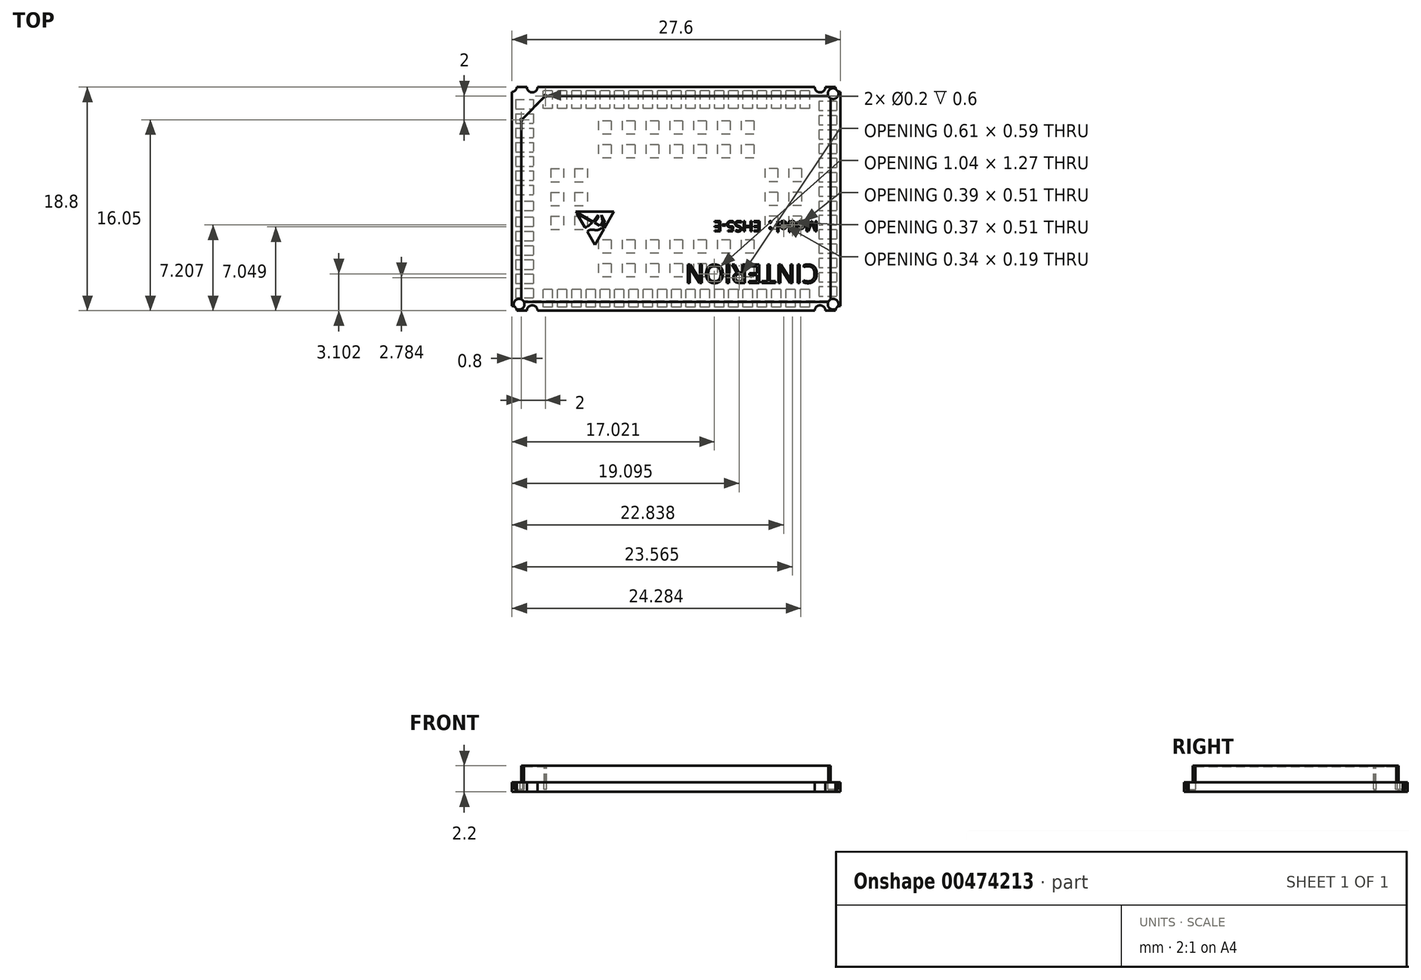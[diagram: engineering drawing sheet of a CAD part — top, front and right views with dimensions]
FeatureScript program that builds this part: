
annotation { "Feature Type Name" : "Feature", "Feature Type Description" : "" }
export const myFeature = defineFeature(function(context is Context, id is Id, definition is map)
    precondition{}
    {
        {
            var Q0;
            Q0=qCreatedBy(makeId("Top.planeOp"),FACE);
            var sketch = newSketch(context, id + "F0", { "sketchPlane" : qUnion([Q0])});
            skLineSegment(sketch, "E0.bottom", {"start": v(13, -8.65) * mm, "end": v(-13, -8.65) * mm});
            skLineSegment(sketch, "E0.top", {"start": v(13, 8.65) * mm, "end": v(-13, 8.65) * mm});
            skLineSegment(sketch, "E0.left", {"start": v(13, -8.65) * mm, "end": v(13, 8.65) * mm});
            skLineSegment(sketch, "E0.right", {"start": v(-13, -8.65) * mm, "end": v(-13, 8.65) * mm});
            skPoint(sketch, "E0.middle", {"position": v(0, 0) * mm});
            skLineSegment(sketch, "E1", {"start": v(-13, 6.65) * mm, "end": v(-11, 8.65) * mm});
            skLineSegment(sketch, "E2", {"start": v(-13, -9.4) * mm, "end": v(-13.8, -9.4) * mm});
            skLineSegment(sketch, "E3", {"start": v(-13.8, -9.4) * mm, "end": v(-13.8, 9.4) * mm});
            skLineSegment(sketch, "E4", {"start": v(-13.8, 9.4) * mm, "end": v(13.8, 9.4) * mm});
            skLineSegment(sketch, "E5", {"start": v(13.8, 9.4) * mm, "end": v(13.8, -9.4) * mm});
            skLineSegment(sketch, "E6", {"start": v(13.8, -9.4) * mm, "end": v(-13.8, -9.4) * mm});
            skArc(sketch, "E7", {"start": v(-13.8, 9) * mm, "mid": v(-13.52, 9.12) * mm, "end": v(-13.4, 9.4) * mm});
            skLineSegment(sketch, "E8", {"start": v(-13.8, 9.4) * mm, "end": v(-12.1, 9.4) * mm});
            skArc(sketch, "E9", {"start": v(-11.65, 9.4) * mm, "mid": v(-12.1, 8.95) * mm, "end": v(-12.55, 9.4) * mm});
            skPoint(sketch, "E10.startSnap0", {"position": v(-12.1, 8.95) * mm});
            skArc(sketch, "E11", {"start": v(13.8, 9) * mm, "mid": v(13.52, 9.12) * mm, "end": v(13.4, 9.4) * mm});
            skArc(sketch, "E12", {"start": v(13.4, -9.4) * mm, "mid": v(13.52, -9.12) * mm, "end": v(13.8, -9) * mm});
            skArc(sketch, "E13", {"start": v(-13.8, -9) * mm, "mid": v(-13.52, -9.12) * mm, "end": v(-13.4, -9.4) * mm});
            skLineSegment(sketch, "E14", {"start": v(-13.8, -9.4) * mm, "end": v(-12.1, -9.4) * mm});
            skLineSegment(sketch, "E15", {"start": v(13.8, -9.4) * mm, "end": v(12.1, -9.4) * mm});
            skLineSegment(sketch, "E16", {"start": v(13.8, 9.4) * mm, "end": v(12.1, 9.4) * mm});
            skArc(sketch, "E17", {"start": v(11.65, 9.4) * mm, "mid": v(12.1, 8.95) * mm, "end": v(12.55, 9.4) * mm});
            skArc(sketch, "E18", {"start": v(12.55, -9.4) * mm, "mid": v(12.1, -8.95) * mm, "end": v(11.65, -9.4) * mm});
            skArc(sketch, "E19", {"start": v(-11.65, -9.4) * mm, "mid": v(-12.1, -8.95) * mm, "end": v(-12.55, -9.4) * mm});
            skSolve(sketch);
        }
        {
            var Q0;
            {var subQ1=sQuery(id+"F0.wireOp",EDGE,"E0.bottom");Q0=makeQuery(id+"F0.imprint","IMPRINT",FACE,{"disambiguationData":[TD([[makeQuery(id+"F0.imprint","IMPRINT",EDGE,{"derivedFrom":subQ1}),-1.0]])]});}
            extrude(context, id + "F1", {"entities" : qUnion([Q0]), "depth" : 1.4 * mm});
        }
        {
            var Q0;
            {var subQ14=sQuery(id+"F0.wireOp",EDGE,"E0.bottom");Q0=makeQuery(id+"F0.imprint","IMPRINT",FACE,{"disambiguationData":[TD([[makeQuery(id+"F0.imprint","IMPRINT",EDGE,{"derivedFrom":subQ14}),1.0]])]});}
            var Q1;
            {var subQ1=sQuery(id+"F0.wireOp",EDGE,"E0.bottom");Q1=makeQuery(id+"F0.imprint","IMPRINT",FACE,{"disambiguationData":[TD([[makeQuery(id+"F0.imprint","IMPRINT",EDGE,{"derivedFrom":subQ1}),-1.0]])]});}
            var Q2;
            {var subQ3=sQuery(id+"F0.wireOp",EDGE,"E1");Q2=makeQuery(id+"F0.imprint","IMPRINT",FACE,{"disambiguationData":[TD([[makeQuery(id+"F0.imprint","IMPRINT",EDGE,{"derivedFrom":subQ3}),1.0]])]});}
            extrude(context, id + "F2", {"entities" : qUnion([Q0, Q1, Q2]), "oppositeDirection" : true, "depth" : 0.8 * mm});
        }
        {
            var Q0;
            Q0=makeQuery(id+"F1.opExtrude","CAP_FACE",FACE,{"disambiguationData":[OSD([sQuery(id+"F0.wireOp",EDGE,"E0.bottom"),sQuery(id+"F0.wireOp",EDGE,"E0.top"),sQuery(id+"F0.wireOp",EDGE,"E0.left"),sQuery(id+"F0.wireOp",EDGE,"E0.right"),sQuery(id+"F0.wireOp",EDGE,"E1")])],"isStart":true});
            shell(context, id + "F3", {"entities" : qUnion([Q0]), "thickness" : 0.05 * mm});
        }
        {
            var Q0;
            Q0=makeQuery(id+"F1.opExtrude","CAP_FACE",FACE,{"disambiguationData":[OSD([sQuery(id+"F0.wireOp",EDGE,"E0.bottom"),sQuery(id+"F0.wireOp",EDGE,"E0.top"),sQuery(id+"F0.wireOp",EDGE,"E0.left"),sQuery(id+"F0.wireOp",EDGE,"E0.right"),sQuery(id+"F0.wireOp",EDGE,"E1")])],"isStart":false});
            var sketch = newSketch(context, id + "F4", { "sketchPlane" : qUnion([Q0])});
            skCircle(sketch, "E20", {"center": v(13.2, -8.85) * mm, "radius": 0.45 * mm});
            skCircle(sketch, "E21.1.0.0", {"center": v(-13.2, -8.85) * mm, "radius": 0.45 * mm});
            skLineSegment(sketch, "E21.direction1", {"start": v(13.2, -8.85) * mm, "end": v(-13.2, -8.85) * mm, "construction": true});
            skCircle(sketch, "E22", {"center": v(-13, 6.65) * mm, "radius": 0.1 * mm});
            skCircle(sketch, "E23", {"center": v(-11, 8.65) * mm, "radius": 0.1 * mm});
            skCircle(sketch, "E24.0.1.0", {"center": v(13.2, 8.85) * mm, "radius": 0.45 * mm});
            skLineSegment(sketch, "E24.direction1", {"start": v(13.2, -8.85) * mm, "end": v(38.2, -8.85) * mm, "construction": true});
            skLineSegment(sketch, "E24.direction2", {"start": v(13.2, -8.85) * mm, "end": v(13.2, 8.85) * mm, "construction": true});
            skSolve(sketch);
        }
        {
            var Q0;
            Q0 = qSketchRegion(id + "F4", true);
            extrude(context, id + "F5", {"entities" : qUnion([Q0]), "operationType" : NewBodyOperationType.REMOVE, "oppositeDirection" : true, "depth" : 2 * mm});
        }
        {
            var Q0;
            Q0=makeQuery(id+"F2.opExtrude","CAP_FACE",FACE,{"disambiguationData":[OSD([sQuery(id+"F0.wireOp",EDGE,"E3"),sQuery(id+"F0.wireOp",EDGE,"E4"),sQuery(id+"F0.wireOp",EDGE,"E5"),sQuery(id+"F0.wireOp",EDGE,"E6"),sQuery(id+"F0.wireOp",EDGE,"E7"),sQuery(id+"F0.wireOp",EDGE,"E8"),sQuery(id+"F0.wireOp",EDGE,"E9"),sQuery(id+"F0.wireOp",EDGE,"E11"),sQuery(id+"F0.wireOp",EDGE,"E12"),sQuery(id+"F0.wireOp",EDGE,"E13"),sQuery(id+"F0.wireOp",EDGE,"E14"),sQuery(id+"F0.wireOp",EDGE,"E15"),sQuery(id+"F0.wireOp",EDGE,"E16"),sQuery(id+"F0.wireOp",EDGE,"E17"),sQuery(id+"F0.wireOp",EDGE,"E18"),sQuery(id+"F0.wireOp",EDGE,"E19")])],"isStart":false});
            var sketch = newSketch(context, id + "F6", { "sketchPlane" : qUnion([Q0])});
            skLineSegment(sketch, "E25.bottom", {"start": v(0.4, 7.6) * mm, "end": v(-0.4, 7.6) * mm});
            skLineSegment(sketch, "E25.top", {"start": v(0.4, 9.1) * mm, "end": v(-0.4, 9.1) * mm});
            skLineSegment(sketch, "E25.left", {"start": v(0.4, 7.6) * mm, "end": v(0.4, 9.1) * mm});
            skLineSegment(sketch, "E25.right", {"start": v(-0.4, 7.6) * mm, "end": v(-0.4, 9.1) * mm});
            skPoint(sketch, "E25.middle", {"position": v(0, 8.35) * mm});
            skLineSegment(sketch, "E26.bottom", {"start": v(0.4, -9.1) * mm, "end": v(-0.4, -9.1) * mm});
            skLineSegment(sketch, "E26.top", {"start": v(0.4, -7.6) * mm, "end": v(-0.4, -7.6) * mm});
            skLineSegment(sketch, "E26.left", {"start": v(0.4, -9.1) * mm, "end": v(0.4, -7.6) * mm});
            skLineSegment(sketch, "E26.right", {"start": v(-0.4, -9.1) * mm, "end": v(-0.4, -7.6) * mm});
            skPoint(sketch, "E26.middle", {"position": v(0, -8.35) * mm});
            skLineSegment(sketch, "E27.1.0.0", {"start": v(-1.6, 7.6) * mm, "end": v(-1.6, 9.1) * mm});
            skLineSegment(sketch, "E27.1.0.1", {"start": v(-0.8, 7.6) * mm, "end": v(-0.8, 9.1) * mm});
            skLineSegment(sketch, "E27.1.0.2", {"start": v(-0.8, 9.1) * mm, "end": v(-1.6, 9.1) * mm});
            skLineSegment(sketch, "E27.1.0.3", {"start": v(-0.8, 7.6) * mm, "end": v(-1.6, 7.6) * mm});
            skPoint(sketch, "E27.1.0.4", {"position": v(-1.2, 8.35) * mm});
            skLineSegment(sketch, "E27.1.0.5", {"start": v(-1.6, -9.1) * mm, "end": v(-1.6, -7.6) * mm});
            skLineSegment(sketch, "E27.1.0.6", {"start": v(-0.8, -9.1) * mm, "end": v(-0.8, -7.6) * mm});
            skLineSegment(sketch, "E27.1.0.7", {"start": v(-0.8, -7.6) * mm, "end": v(-1.6, -7.6) * mm});
            skLineSegment(sketch, "E27.1.0.8", {"start": v(-0.8, -9.1) * mm, "end": v(-1.6, -9.1) * mm});
            skPoint(sketch, "E27.1.0.9", {"position": v(-1.2, -8.35) * mm});
            skLineSegment(sketch, "E27.2.0.0", {"start": v(-2.8, 7.6) * mm, "end": v(-2.8, 9.1) * mm});
            skLineSegment(sketch, "E27.2.0.1", {"start": v(-2, 7.6) * mm, "end": v(-2, 9.1) * mm});
            skLineSegment(sketch, "E27.2.0.2", {"start": v(-2, 9.1) * mm, "end": v(-2.8, 9.1) * mm});
            skLineSegment(sketch, "E27.2.0.3", {"start": v(-2, 7.6) * mm, "end": v(-2.8, 7.6) * mm});
            skPoint(sketch, "E27.2.0.4", {"position": v(-2.4, 8.35) * mm});
            skLineSegment(sketch, "E27.2.0.5", {"start": v(-2.8, -9.1) * mm, "end": v(-2.8, -7.6) * mm});
            skLineSegment(sketch, "E27.2.0.6", {"start": v(-2, -9.1) * mm, "end": v(-2, -7.6) * mm});
            skLineSegment(sketch, "E27.2.0.7", {"start": v(-2, -7.6) * mm, "end": v(-2.8, -7.6) * mm});
            skLineSegment(sketch, "E27.2.0.8", {"start": v(-2, -9.1) * mm, "end": v(-2.8, -9.1) * mm});
            skPoint(sketch, "E27.2.0.9", {"position": v(-2.4, -8.35) * mm});
            skLineSegment(sketch, "E27.3.0.0", {"start": v(-4, 7.6) * mm, "end": v(-4, 9.1) * mm});
            skLineSegment(sketch, "E27.3.0.1", {"start": v(-3.2, 7.6) * mm, "end": v(-3.2, 9.1) * mm});
            skLineSegment(sketch, "E27.3.0.2", {"start": v(-3.2, 9.1) * mm, "end": v(-4, 9.1) * mm});
            skLineSegment(sketch, "E27.3.0.3", {"start": v(-3.2, 7.6) * mm, "end": v(-4, 7.6) * mm});
            skPoint(sketch, "E27.3.0.4", {"position": v(-3.6, 8.35) * mm});
            skLineSegment(sketch, "E27.3.0.5", {"start": v(-4, -9.1) * mm, "end": v(-4, -7.6) * mm});
            skLineSegment(sketch, "E27.3.0.6", {"start": v(-3.2, -9.1) * mm, "end": v(-3.2, -7.6) * mm});
            skLineSegment(sketch, "E27.3.0.7", {"start": v(-3.2, -7.6) * mm, "end": v(-4, -7.6) * mm});
            skLineSegment(sketch, "E27.3.0.8", {"start": v(-3.2, -9.1) * mm, "end": v(-4, -9.1) * mm});
            skPoint(sketch, "E27.3.0.9", {"position": v(-3.6, -8.35) * mm});
            skLineSegment(sketch, "E27.4.0.0", {"start": v(-5.2, 7.6) * mm, "end": v(-5.2, 9.1) * mm});
            skLineSegment(sketch, "E27.4.0.1", {"start": v(-4.4, 7.6) * mm, "end": v(-4.4, 9.1) * mm});
            skLineSegment(sketch, "E27.4.0.2", {"start": v(-4.4, 9.1) * mm, "end": v(-5.2, 9.1) * mm});
            skLineSegment(sketch, "E27.4.0.3", {"start": v(-4.4, 7.6) * mm, "end": v(-5.2, 7.6) * mm});
            skPoint(sketch, "E27.4.0.4", {"position": v(-4.8, 8.35) * mm});
            skLineSegment(sketch, "E27.4.0.5", {"start": v(-5.2, -9.1) * mm, "end": v(-5.2, -7.6) * mm});
            skLineSegment(sketch, "E27.4.0.6", {"start": v(-4.4, -9.1) * mm, "end": v(-4.4, -7.6) * mm});
            skLineSegment(sketch, "E27.4.0.7", {"start": v(-4.4, -7.6) * mm, "end": v(-5.2, -7.6) * mm});
            skLineSegment(sketch, "E27.4.0.8", {"start": v(-4.4, -9.1) * mm, "end": v(-5.2, -9.1) * mm});
            skPoint(sketch, "E27.4.0.9", {"position": v(-4.8, -8.35) * mm});
            skLineSegment(sketch, "E27.5.0.0", {"start": v(-6.4, 7.6) * mm, "end": v(-6.4, 9.1) * mm});
            skLineSegment(sketch, "E27.5.0.1", {"start": v(-5.6, 7.6) * mm, "end": v(-5.6, 9.1) * mm});
            skLineSegment(sketch, "E27.5.0.2", {"start": v(-5.6, 9.1) * mm, "end": v(-6.4, 9.1) * mm});
            skLineSegment(sketch, "E27.5.0.3", {"start": v(-5.6, 7.6) * mm, "end": v(-6.4, 7.6) * mm});
            skPoint(sketch, "E27.5.0.4", {"position": v(-6, 8.35) * mm});
            skLineSegment(sketch, "E27.5.0.5", {"start": v(-6.4, -9.1) * mm, "end": v(-6.4, -7.6) * mm});
            skLineSegment(sketch, "E27.5.0.6", {"start": v(-5.6, -9.1) * mm, "end": v(-5.6, -7.6) * mm});
            skLineSegment(sketch, "E27.5.0.7", {"start": v(-5.6, -7.6) * mm, "end": v(-6.4, -7.6) * mm});
            skLineSegment(sketch, "E27.5.0.8", {"start": v(-5.6, -9.1) * mm, "end": v(-6.4, -9.1) * mm});
            skPoint(sketch, "E27.5.0.9", {"position": v(-6, -8.35) * mm});
            skLineSegment(sketch, "E27.6.0.0", {"start": v(-7.6, 7.6) * mm, "end": v(-7.6, 9.1) * mm});
            skLineSegment(sketch, "E27.6.0.1", {"start": v(-6.8, 7.6) * mm, "end": v(-6.8, 9.1) * mm});
            skLineSegment(sketch, "E27.6.0.2", {"start": v(-6.8, 9.1) * mm, "end": v(-7.6, 9.1) * mm});
            skLineSegment(sketch, "E27.6.0.3", {"start": v(-6.8, 7.6) * mm, "end": v(-7.6, 7.6) * mm});
            skPoint(sketch, "E27.6.0.4", {"position": v(-7.2, 8.35) * mm});
            skLineSegment(sketch, "E27.6.0.5", {"start": v(-7.6, -9.1) * mm, "end": v(-7.6, -7.6) * mm});
            skLineSegment(sketch, "E27.6.0.6", {"start": v(-6.8, -9.1) * mm, "end": v(-6.8, -7.6) * mm});
            skLineSegment(sketch, "E27.6.0.7", {"start": v(-6.8, -7.6) * mm, "end": v(-7.6, -7.6) * mm});
            skLineSegment(sketch, "E27.6.0.8", {"start": v(-6.8, -9.1) * mm, "end": v(-7.6, -9.1) * mm});
            skPoint(sketch, "E27.6.0.9", {"position": v(-7.2, -8.35) * mm});
            skLineSegment(sketch, "E27.7.0.0", {"start": v(-8.8, 7.6) * mm, "end": v(-8.8, 9.1) * mm});
            skLineSegment(sketch, "E27.7.0.1", {"start": v(-8, 7.6) * mm, "end": v(-8, 9.1) * mm});
            skLineSegment(sketch, "E27.7.0.2", {"start": v(-8, 9.1) * mm, "end": v(-8.8, 9.1) * mm});
            skLineSegment(sketch, "E27.7.0.3", {"start": v(-8, 7.6) * mm, "end": v(-8.8, 7.6) * mm});
            skPoint(sketch, "E27.7.0.4", {"position": v(-8.4, 8.35) * mm});
            skLineSegment(sketch, "E27.7.0.5", {"start": v(-8.8, -9.1) * mm, "end": v(-8.8, -7.6) * mm});
            skLineSegment(sketch, "E27.7.0.6", {"start": v(-8, -9.1) * mm, "end": v(-8, -7.6) * mm});
            skLineSegment(sketch, "E27.7.0.7", {"start": v(-8, -7.6) * mm, "end": v(-8.8, -7.6) * mm});
            skLineSegment(sketch, "E27.7.0.8", {"start": v(-8, -9.1) * mm, "end": v(-8.8, -9.1) * mm});
            skPoint(sketch, "E27.7.0.9", {"position": v(-8.4, -8.35) * mm});
            skLineSegment(sketch, "E27.8.0.0", {"start": v(-10, 7.6) * mm, "end": v(-10, 9.1) * mm});
            skLineSegment(sketch, "E27.8.0.1", {"start": v(-9.2, 7.6) * mm, "end": v(-9.2, 9.1) * mm});
            skLineSegment(sketch, "E27.8.0.2", {"start": v(-9.2, 9.1) * mm, "end": v(-10, 9.1) * mm});
            skLineSegment(sketch, "E27.8.0.3", {"start": v(-9.2, 7.6) * mm, "end": v(-10, 7.6) * mm});
            skPoint(sketch, "E27.8.0.4", {"position": v(-9.6, 8.35) * mm});
            skLineSegment(sketch, "E27.8.0.5", {"start": v(-10, -9.1) * mm, "end": v(-10, -7.6) * mm});
            skLineSegment(sketch, "E27.8.0.6", {"start": v(-9.2, -9.1) * mm, "end": v(-9.2, -7.6) * mm});
            skLineSegment(sketch, "E27.8.0.7", {"start": v(-9.2, -7.6) * mm, "end": v(-10, -7.6) * mm});
            skLineSegment(sketch, "E27.8.0.8", {"start": v(-9.2, -9.1) * mm, "end": v(-10, -9.1) * mm});
            skPoint(sketch, "E27.8.0.9", {"position": v(-9.6, -8.35) * mm});
            skLineSegment(sketch, "E27.9.0.0", {"start": v(-11.2, 7.6) * mm, "end": v(-11.2, 9.1) * mm});
            skLineSegment(sketch, "E27.9.0.1", {"start": v(-10.4, 7.6) * mm, "end": v(-10.4, 9.1) * mm});
            skLineSegment(sketch, "E27.9.0.2", {"start": v(-10.4, 9.1) * mm, "end": v(-11.2, 9.1) * mm});
            skLineSegment(sketch, "E27.9.0.3", {"start": v(-10.4, 7.6) * mm, "end": v(-11.2, 7.6) * mm});
            skPoint(sketch, "E27.9.0.4", {"position": v(-10.8, 8.35) * mm});
            skLineSegment(sketch, "E27.9.0.5", {"start": v(-11.2, -9.1) * mm, "end": v(-11.2, -7.6) * mm});
            skLineSegment(sketch, "E27.9.0.6", {"start": v(-10.4, -9.1) * mm, "end": v(-10.4, -7.6) * mm});
            skLineSegment(sketch, "E27.9.0.7", {"start": v(-10.4, -7.6) * mm, "end": v(-11.2, -7.6) * mm});
            skLineSegment(sketch, "E27.9.0.8", {"start": v(-10.4, -9.1) * mm, "end": v(-11.2, -9.1) * mm});
            skPoint(sketch, "E27.9.0.9", {"position": v(-10.8, -8.35) * mm});
            skLineSegment(sketch, "E27.direction1", {"start": v(-0.4, -9.1) * mm, "end": v(-1.6, -9.1) * mm, "construction": true});
            skLineSegment(sketch, "E28.1.0.0", {"start": v(0.8, 7.6) * mm, "end": v(0.8, 9.1) * mm});
            skLineSegment(sketch, "E28.1.0.1", {"start": v(1.6, 7.6) * mm, "end": v(1.6, 9.1) * mm});
            skLineSegment(sketch, "E28.1.0.2", {"start": v(1.6, 9.1) * mm, "end": v(0.8, 9.1) * mm});
            skLineSegment(sketch, "E28.1.0.3", {"start": v(1.6, 7.6) * mm, "end": v(0.8, 7.6) * mm});
            skPoint(sketch, "E28.1.0.4", {"position": v(1.2, 8.35) * mm});
            skLineSegment(sketch, "E28.1.0.5", {"start": v(1.6, -9.1) * mm, "end": v(0.8, -9.1) * mm});
            skLineSegment(sketch, "E28.1.0.6", {"start": v(1.6, -7.6) * mm, "end": v(0.8, -7.6) * mm});
            skPoint(sketch, "E28.1.0.7", {"position": v(1.2, -8.35) * mm});
            skLineSegment(sketch, "E28.1.0.8", {"start": v(0.8, -9.1) * mm, "end": v(0.8, -7.6) * mm});
            skLineSegment(sketch, "E28.1.0.9", {"start": v(1.6, -9.1) * mm, "end": v(1.6, -7.6) * mm});
            skLineSegment(sketch, "E28.2.0.0", {"start": v(2, 7.6) * mm, "end": v(2, 9.1) * mm});
            skLineSegment(sketch, "E28.2.0.1", {"start": v(2.8, 7.6) * mm, "end": v(2.8, 9.1) * mm});
            skLineSegment(sketch, "E28.2.0.2", {"start": v(2.8, 9.1) * mm, "end": v(2, 9.1) * mm});
            skLineSegment(sketch, "E28.2.0.3", {"start": v(2.8, 7.6) * mm, "end": v(2, 7.6) * mm});
            skPoint(sketch, "E28.2.0.4", {"position": v(2.4, 8.35) * mm});
            skLineSegment(sketch, "E28.2.0.5", {"start": v(2.8, -9.1) * mm, "end": v(2, -9.1) * mm});
            skLineSegment(sketch, "E28.2.0.6", {"start": v(2.8, -7.6) * mm, "end": v(2, -7.6) * mm});
            skPoint(sketch, "E28.2.0.7", {"position": v(2.4, -8.35) * mm});
            skLineSegment(sketch, "E28.2.0.8", {"start": v(2, -9.1) * mm, "end": v(2, -7.6) * mm});
            skLineSegment(sketch, "E28.2.0.9", {"start": v(2.8, -9.1) * mm, "end": v(2.8, -7.6) * mm});
            skLineSegment(sketch, "E28.3.0.0", {"start": v(3.2, 7.6) * mm, "end": v(3.2, 9.1) * mm});
            skLineSegment(sketch, "E28.3.0.1", {"start": v(4, 7.6) * mm, "end": v(4, 9.1) * mm});
            skLineSegment(sketch, "E28.3.0.2", {"start": v(4, 9.1) * mm, "end": v(3.2, 9.1) * mm});
            skLineSegment(sketch, "E28.3.0.3", {"start": v(4, 7.6) * mm, "end": v(3.2, 7.6) * mm});
            skPoint(sketch, "E28.3.0.4", {"position": v(3.6, 8.35) * mm});
            skLineSegment(sketch, "E28.3.0.5", {"start": v(4, -9.1) * mm, "end": v(3.2, -9.1) * mm});
            skLineSegment(sketch, "E28.3.0.6", {"start": v(4, -7.6) * mm, "end": v(3.2, -7.6) * mm});
            skPoint(sketch, "E28.3.0.7", {"position": v(3.6, -8.35) * mm});
            skLineSegment(sketch, "E28.3.0.8", {"start": v(3.2, -9.1) * mm, "end": v(3.2, -7.6) * mm});
            skLineSegment(sketch, "E28.3.0.9", {"start": v(4, -9.1) * mm, "end": v(4, -7.6) * mm});
            skLineSegment(sketch, "E28.4.0.0", {"start": v(4.4, 7.6) * mm, "end": v(4.4, 9.1) * mm});
            skLineSegment(sketch, "E28.4.0.1", {"start": v(5.2, 7.6) * mm, "end": v(5.2, 9.1) * mm});
            skLineSegment(sketch, "E28.4.0.2", {"start": v(5.2, 9.1) * mm, "end": v(4.4, 9.1) * mm});
            skLineSegment(sketch, "E28.4.0.3", {"start": v(5.2, 7.6) * mm, "end": v(4.4, 7.6) * mm});
            skPoint(sketch, "E28.4.0.4", {"position": v(4.8, 8.35) * mm});
            skLineSegment(sketch, "E28.4.0.5", {"start": v(5.2, -9.1) * mm, "end": v(4.4, -9.1) * mm});
            skLineSegment(sketch, "E28.4.0.6", {"start": v(5.2, -7.6) * mm, "end": v(4.4, -7.6) * mm});
            skPoint(sketch, "E28.4.0.7", {"position": v(4.8, -8.35) * mm});
            skLineSegment(sketch, "E28.4.0.8", {"start": v(4.4, -9.1) * mm, "end": v(4.4, -7.6) * mm});
            skLineSegment(sketch, "E28.4.0.9", {"start": v(5.2, -9.1) * mm, "end": v(5.2, -7.6) * mm});
            skLineSegment(sketch, "E28.5.0.0", {"start": v(5.6, 7.6) * mm, "end": v(5.6, 9.1) * mm});
            skLineSegment(sketch, "E28.5.0.1", {"start": v(6.4, 7.6) * mm, "end": v(6.4, 9.1) * mm});
            skLineSegment(sketch, "E28.5.0.2", {"start": v(6.4, 9.1) * mm, "end": v(5.6, 9.1) * mm});
            skLineSegment(sketch, "E28.5.0.3", {"start": v(6.4, 7.6) * mm, "end": v(5.6, 7.6) * mm});
            skPoint(sketch, "E28.5.0.4", {"position": v(6, 8.35) * mm});
            skLineSegment(sketch, "E28.5.0.5", {"start": v(6.4, -9.1) * mm, "end": v(5.6, -9.1) * mm});
            skLineSegment(sketch, "E28.5.0.6", {"start": v(6.4, -7.6) * mm, "end": v(5.6, -7.6) * mm});
            skPoint(sketch, "E28.5.0.7", {"position": v(6, -8.35) * mm});
            skLineSegment(sketch, "E28.5.0.8", {"start": v(5.6, -9.1) * mm, "end": v(5.6, -7.6) * mm});
            skLineSegment(sketch, "E28.5.0.9", {"start": v(6.4, -9.1) * mm, "end": v(6.4, -7.6) * mm});
            skLineSegment(sketch, "E28.6.0.0", {"start": v(6.8, 7.6) * mm, "end": v(6.8, 9.1) * mm});
            skLineSegment(sketch, "E28.6.0.1", {"start": v(7.6, 7.6) * mm, "end": v(7.6, 9.1) * mm});
            skLineSegment(sketch, "E28.6.0.2", {"start": v(7.6, 9.1) * mm, "end": v(6.8, 9.1) * mm});
            skLineSegment(sketch, "E28.6.0.3", {"start": v(7.6, 7.6) * mm, "end": v(6.8, 7.6) * mm});
            skPoint(sketch, "E28.6.0.4", {"position": v(7.2, 8.35) * mm});
            skLineSegment(sketch, "E28.6.0.5", {"start": v(7.6, -9.1) * mm, "end": v(6.8, -9.1) * mm});
            skLineSegment(sketch, "E28.6.0.6", {"start": v(7.6, -7.6) * mm, "end": v(6.8, -7.6) * mm});
            skPoint(sketch, "E28.6.0.7", {"position": v(7.2, -8.35) * mm});
            skLineSegment(sketch, "E28.6.0.8", {"start": v(6.8, -9.1) * mm, "end": v(6.8, -7.6) * mm});
            skLineSegment(sketch, "E28.6.0.9", {"start": v(7.6, -9.1) * mm, "end": v(7.6, -7.6) * mm});
            skLineSegment(sketch, "E28.7.0.0", {"start": v(8, 7.6) * mm, "end": v(8, 9.1) * mm});
            skLineSegment(sketch, "E28.7.0.1", {"start": v(8.8, 7.6) * mm, "end": v(8.8, 9.1) * mm});
            skLineSegment(sketch, "E28.7.0.2", {"start": v(8.8, 9.1) * mm, "end": v(8, 9.1) * mm});
            skLineSegment(sketch, "E28.7.0.3", {"start": v(8.8, 7.6) * mm, "end": v(8, 7.6) * mm});
            skPoint(sketch, "E28.7.0.4", {"position": v(8.4, 8.35) * mm});
            skLineSegment(sketch, "E28.7.0.5", {"start": v(8.8, -9.1) * mm, "end": v(8, -9.1) * mm});
            skLineSegment(sketch, "E28.7.0.6", {"start": v(8.8, -7.6) * mm, "end": v(8, -7.6) * mm});
            skPoint(sketch, "E28.7.0.7", {"position": v(8.4, -8.35) * mm});
            skLineSegment(sketch, "E28.7.0.8", {"start": v(8, -9.1) * mm, "end": v(8, -7.6) * mm});
            skLineSegment(sketch, "E28.7.0.9", {"start": v(8.8, -9.1) * mm, "end": v(8.8, -7.6) * mm});
            skLineSegment(sketch, "E28.8.0.0", {"start": v(9.2, 7.6) * mm, "end": v(9.2, 9.1) * mm});
            skLineSegment(sketch, "E28.8.0.1", {"start": v(10, 7.6) * mm, "end": v(10, 9.1) * mm});
            skLineSegment(sketch, "E28.8.0.2", {"start": v(10, 9.1) * mm, "end": v(9.2, 9.1) * mm});
            skLineSegment(sketch, "E28.8.0.3", {"start": v(10, 7.6) * mm, "end": v(9.2, 7.6) * mm});
            skPoint(sketch, "E28.8.0.4", {"position": v(9.6, 8.35) * mm});
            skLineSegment(sketch, "E28.8.0.5", {"start": v(10, -9.1) * mm, "end": v(9.2, -9.1) * mm});
            skLineSegment(sketch, "E28.8.0.6", {"start": v(10, -7.6) * mm, "end": v(9.2, -7.6) * mm});
            skPoint(sketch, "E28.8.0.7", {"position": v(9.6, -8.35) * mm});
            skLineSegment(sketch, "E28.8.0.8", {"start": v(9.2, -9.1) * mm, "end": v(9.2, -7.6) * mm});
            skLineSegment(sketch, "E28.8.0.9", {"start": v(10, -9.1) * mm, "end": v(10, -7.6) * mm});
            skLineSegment(sketch, "E28.9.0.0", {"start": v(10.4, 7.6) * mm, "end": v(10.4, 9.1) * mm});
            skLineSegment(sketch, "E28.9.0.1", {"start": v(11.2, 7.6) * mm, "end": v(11.2, 9.1) * mm});
            skLineSegment(sketch, "E28.9.0.2", {"start": v(11.2, 9.1) * mm, "end": v(10.4, 9.1) * mm});
            skLineSegment(sketch, "E28.9.0.3", {"start": v(11.2, 7.6) * mm, "end": v(10.4, 7.6) * mm});
            skPoint(sketch, "E28.9.0.4", {"position": v(10.8, 8.35) * mm});
            skLineSegment(sketch, "E28.9.0.5", {"start": v(11.2, -9.1) * mm, "end": v(10.4, -9.1) * mm});
            skLineSegment(sketch, "E28.9.0.6", {"start": v(11.2, -7.6) * mm, "end": v(10.4, -7.6) * mm});
            skPoint(sketch, "E28.9.0.7", {"position": v(10.8, -8.35) * mm});
            skLineSegment(sketch, "E28.9.0.8", {"start": v(10.4, -9.1) * mm, "end": v(10.4, -7.6) * mm});
            skLineSegment(sketch, "E28.9.0.9", {"start": v(11.2, -9.1) * mm, "end": v(11.2, -7.6) * mm});
            skLineSegment(sketch, "E28.direction1", {"start": v(-0.4, -9.1) * mm, "end": v(0.8, -9.1) * mm, "construction": true});
            skLineSegment(sketch, "E29.bottom", {"start": v(0.55, -6.55) * mm, "end": v(-0.55, -6.55) * mm});
            skLineSegment(sketch, "E29.top", {"start": v(0.55, -5.45) * mm, "end": v(-0.55, -5.45) * mm});
            skLineSegment(sketch, "E29.left", {"start": v(0.55, -6.55) * mm, "end": v(0.55, -5.45) * mm});
            skLineSegment(sketch, "E29.right", {"start": v(-0.55, -6.55) * mm, "end": v(-0.55, -5.45) * mm});
            skPoint(sketch, "E29.middle", {"position": v(0, -6) * mm});
            skLineSegment(sketch, "E30.bottom", {"start": v(0.55, -4.55) * mm, "end": v(-0.55, -4.55) * mm});
            skLineSegment(sketch, "E30.top", {"start": v(0.55, -3.45) * mm, "end": v(-0.55, -3.45) * mm});
            skLineSegment(sketch, "E30.left", {"start": v(0.55, -4.55) * mm, "end": v(0.55, -3.45) * mm});
            skLineSegment(sketch, "E30.right", {"start": v(-0.55, -4.55) * mm, "end": v(-0.55, -3.45) * mm});
            skPoint(sketch, "E30.middle", {"position": v(0, -4) * mm});
            skPoint(sketch, "E30.cornerSnap0", {"position": v(0.55, -6) * mm});
            skLineSegment(sketch, "E31.bottom", {"start": v(0.55, 3.45) * mm, "end": v(-0.55, 3.45) * mm});
            skLineSegment(sketch, "E31.top", {"start": v(0.55, 4.55) * mm, "end": v(-0.55, 4.55) * mm});
            skLineSegment(sketch, "E31.left", {"start": v(0.55, 3.45) * mm, "end": v(0.55, 4.55) * mm});
            skLineSegment(sketch, "E31.right", {"start": v(-0.55, 3.45) * mm, "end": v(-0.55, 4.55) * mm});
            skPoint(sketch, "E31.middle", {"position": v(0, 4) * mm});
            skLineSegment(sketch, "E32.bottom", {"start": v(0.55, 5.45) * mm, "end": v(-0.55, 5.45) * mm});
            skLineSegment(sketch, "E32.top", {"start": v(0.55, 6.55) * mm, "end": v(-0.55, 6.55) * mm});
            skLineSegment(sketch, "E32.left", {"start": v(0.55, 5.45) * mm, "end": v(0.55, 6.55) * mm});
            skLineSegment(sketch, "E32.right", {"start": v(-0.55, 5.45) * mm, "end": v(-0.55, 6.55) * mm});
            skPoint(sketch, "E32.middle", {"position": v(0, 6) * mm});
            skLineSegment(sketch, "E33.1.0.0", {"start": v(2.55, 5.45) * mm, "end": v(2.55, 6.55) * mm});
            skLineSegment(sketch, "E33.1.0.1", {"start": v(1.45, 5.45) * mm, "end": v(1.45, 6.55) * mm});
            skLineSegment(sketch, "E33.1.0.2", {"start": v(2.55, 5.45) * mm, "end": v(1.45, 5.45) * mm});
            skPoint(sketch, "E33.1.0.3", {"position": v(2, 6) * mm});
            skLineSegment(sketch, "E33.1.0.4", {"start": v(1.45, 3.45) * mm, "end": v(1.45, 4.55) * mm});
            skLineSegment(sketch, "E33.1.0.5", {"start": v(2.55, 3.45) * mm, "end": v(2.55, 4.55) * mm});
            skLineSegment(sketch, "E33.1.0.6", {"start": v(2.55, 6.55) * mm, "end": v(1.45, 6.55) * mm});
            skLineSegment(sketch, "E33.1.0.7", {"start": v(2.55, 4.55) * mm, "end": v(1.45, 4.55) * mm});
            skLineSegment(sketch, "E33.1.0.8", {"start": v(2.55, 3.45) * mm, "end": v(1.45, 3.45) * mm});
            skPoint(sketch, "E33.1.0.9", {"position": v(2, 4) * mm});
            skLineSegment(sketch, "E33.1.0.10", {"start": v(2.55, -6.55) * mm, "end": v(1.45, -6.55) * mm});
            skLineSegment(sketch, "E33.1.0.11", {"start": v(1.45, -4.55) * mm, "end": v(1.45, -3.45) * mm});
            skLineSegment(sketch, "E33.1.0.12", {"start": v(2.55, -4.55) * mm, "end": v(2.55, -3.45) * mm});
            skPoint(sketch, "E33.1.0.13", {"position": v(2.55, -6) * mm});
            skPoint(sketch, "E33.1.0.14", {"position": v(2, -4) * mm});
            skLineSegment(sketch, "E33.1.0.15", {"start": v(2.55, -3.45) * mm, "end": v(1.45, -3.45) * mm});
            skPoint(sketch, "E33.1.0.16", {"position": v(2, -6) * mm});
            skLineSegment(sketch, "E33.1.0.17", {"start": v(2.55, -4.55) * mm, "end": v(1.45, -4.55) * mm});
            skLineSegment(sketch, "E33.1.0.18", {"start": v(1.45, -6.55) * mm, "end": v(1.45, -5.45) * mm});
            skLineSegment(sketch, "E33.1.0.19", {"start": v(2.55, -6.55) * mm, "end": v(2.55, -5.45) * mm});
            skLineSegment(sketch, "E33.1.0.20", {"start": v(2.55, -5.45) * mm, "end": v(1.45, -5.45) * mm});
            skLineSegment(sketch, "E33.2.0.0", {"start": v(4.55, 5.45) * mm, "end": v(4.55, 6.55) * mm});
            skLineSegment(sketch, "E33.2.0.1", {"start": v(3.45, 5.45) * mm, "end": v(3.45, 6.55) * mm});
            skLineSegment(sketch, "E33.2.0.2", {"start": v(4.55, 5.45) * mm, "end": v(3.45, 5.45) * mm});
            skPoint(sketch, "E33.2.0.3", {"position": v(4, 6) * mm});
            skLineSegment(sketch, "E33.2.0.4", {"start": v(3.45, 3.45) * mm, "end": v(3.45, 4.55) * mm});
            skLineSegment(sketch, "E33.2.0.5", {"start": v(4.55, 3.45) * mm, "end": v(4.55, 4.55) * mm});
            skLineSegment(sketch, "E33.2.0.6", {"start": v(4.55, 6.55) * mm, "end": v(3.45, 6.55) * mm});
            skLineSegment(sketch, "E33.2.0.7", {"start": v(4.55, 4.55) * mm, "end": v(3.45, 4.55) * mm});
            skLineSegment(sketch, "E33.2.0.8", {"start": v(4.55, 3.45) * mm, "end": v(3.45, 3.45) * mm});
            skPoint(sketch, "E33.2.0.9", {"position": v(4, 4) * mm});
            skLineSegment(sketch, "E33.2.0.10", {"start": v(4.55, -6.55) * mm, "end": v(3.45, -6.55) * mm});
            skLineSegment(sketch, "E33.2.0.11", {"start": v(3.45, -4.55) * mm, "end": v(3.45, -3.45) * mm});
            skLineSegment(sketch, "E33.2.0.12", {"start": v(4.55, -4.55) * mm, "end": v(4.55, -3.45) * mm});
            skPoint(sketch, "E33.2.0.13", {"position": v(4.55, -6) * mm});
            skPoint(sketch, "E33.2.0.14", {"position": v(4, -4) * mm});
            skLineSegment(sketch, "E33.2.0.15", {"start": v(4.55, -3.45) * mm, "end": v(3.45, -3.45) * mm});
            skPoint(sketch, "E33.2.0.16", {"position": v(4, -6) * mm});
            skLineSegment(sketch, "E33.2.0.17", {"start": v(4.55, -4.55) * mm, "end": v(3.45, -4.55) * mm});
            skLineSegment(sketch, "E33.2.0.18", {"start": v(3.45, -6.55) * mm, "end": v(3.45, -5.45) * mm});
            skLineSegment(sketch, "E33.2.0.19", {"start": v(4.55, -6.55) * mm, "end": v(4.55, -5.45) * mm});
            skLineSegment(sketch, "E33.2.0.20", {"start": v(4.55, -5.45) * mm, "end": v(3.45, -5.45) * mm});
            skLineSegment(sketch, "E33.3.0.0", {"start": v(6.55, 5.45) * mm, "end": v(6.55, 6.55) * mm});
            skLineSegment(sketch, "E33.3.0.1", {"start": v(5.45, 5.45) * mm, "end": v(5.45, 6.55) * mm});
            skLineSegment(sketch, "E33.3.0.2", {"start": v(6.55, 5.45) * mm, "end": v(5.45, 5.45) * mm});
            skPoint(sketch, "E33.3.0.3", {"position": v(6, 6) * mm});
            skLineSegment(sketch, "E33.3.0.4", {"start": v(5.45, 3.45) * mm, "end": v(5.45, 4.55) * mm});
            skLineSegment(sketch, "E33.3.0.5", {"start": v(6.55, 3.45) * mm, "end": v(6.55, 4.55) * mm});
            skLineSegment(sketch, "E33.3.0.6", {"start": v(6.55, 6.55) * mm, "end": v(5.45, 6.55) * mm});
            skLineSegment(sketch, "E33.3.0.7", {"start": v(6.55, 4.55) * mm, "end": v(5.45, 4.55) * mm});
            skLineSegment(sketch, "E33.3.0.8", {"start": v(6.55, 3.45) * mm, "end": v(5.45, 3.45) * mm});
            skPoint(sketch, "E33.3.0.9", {"position": v(6, 4) * mm});
            skLineSegment(sketch, "E33.3.0.10", {"start": v(6.55, -6.55) * mm, "end": v(5.45, -6.55) * mm});
            skLineSegment(sketch, "E33.3.0.11", {"start": v(5.45, -4.55) * mm, "end": v(5.45, -3.45) * mm});
            skLineSegment(sketch, "E33.3.0.12", {"start": v(6.55, -4.55) * mm, "end": v(6.55, -3.45) * mm});
            skPoint(sketch, "E33.3.0.13", {"position": v(6.55, -6) * mm});
            skPoint(sketch, "E33.3.0.14", {"position": v(6, -4) * mm});
            skLineSegment(sketch, "E33.3.0.15", {"start": v(6.55, -3.45) * mm, "end": v(5.45, -3.45) * mm});
            skPoint(sketch, "E33.3.0.16", {"position": v(6, -6) * mm});
            skLineSegment(sketch, "E33.3.0.17", {"start": v(6.55, -4.55) * mm, "end": v(5.45, -4.55) * mm});
            skLineSegment(sketch, "E33.3.0.18", {"start": v(5.45, -6.55) * mm, "end": v(5.45, -5.45) * mm});
            skLineSegment(sketch, "E33.3.0.19", {"start": v(6.55, -6.55) * mm, "end": v(6.55, -5.45) * mm});
            skLineSegment(sketch, "E33.3.0.20", {"start": v(6.55, -5.45) * mm, "end": v(5.45, -5.45) * mm});
            skLineSegment(sketch, "E33.direction1", {"start": v(-0.55, -6.55) * mm, "end": v(1.45, -6.55) * mm, "construction": true});
            skPoint(sketch, "E34.1.0.0", {"position": v(-2, -6) * mm});
            skLineSegment(sketch, "E34.1.0.1", {"start": v(-1.45, -4.55) * mm, "end": v(-2.55, -4.55) * mm});
            skLineSegment(sketch, "E34.1.0.2", {"start": v(-1.45, -4.55) * mm, "end": v(-1.45, -3.45) * mm});
            skLineSegment(sketch, "E34.1.0.3", {"start": v(-1.45, -3.45) * mm, "end": v(-2.55, -3.45) * mm});
            skPoint(sketch, "E34.1.0.4", {"position": v(-2, -4) * mm});
            skLineSegment(sketch, "E34.1.0.5", {"start": v(-2.55, -4.55) * mm, "end": v(-2.55, -3.45) * mm});
            skLineSegment(sketch, "E34.1.0.6", {"start": v(-2.55, -6.55) * mm, "end": v(-2.55, -5.45) * mm});
            skPoint(sketch, "E34.1.0.7", {"position": v(-1.45, -6) * mm});
            skLineSegment(sketch, "E34.1.0.8", {"start": v(-1.45, -6.55) * mm, "end": v(-1.45, -5.45) * mm});
            skLineSegment(sketch, "E34.1.0.9", {"start": v(-1.45, -6.55) * mm, "end": v(-2.55, -6.55) * mm});
            skLineSegment(sketch, "E34.1.0.10", {"start": v(-1.45, -5.45) * mm, "end": v(-2.55, -5.45) * mm});
            skPoint(sketch, "E34.1.0.11", {"position": v(-2, 6) * mm});
            skLineSegment(sketch, "E34.1.0.12", {"start": v(-1.45, 5.45) * mm, "end": v(-2.55, 5.45) * mm});
            skLineSegment(sketch, "E34.1.0.13", {"start": v(-1.45, 6.55) * mm, "end": v(-2.55, 6.55) * mm});
            skLineSegment(sketch, "E34.1.0.14", {"start": v(-2.55, 5.45) * mm, "end": v(-2.55, 6.55) * mm});
            skLineSegment(sketch, "E34.1.0.15", {"start": v(-1.45, 5.45) * mm, "end": v(-1.45, 6.55) * mm});
            skLineSegment(sketch, "E34.1.0.16", {"start": v(-1.45, 3.45) * mm, "end": v(-2.55, 3.45) * mm});
            skPoint(sketch, "E34.1.0.17", {"position": v(-2, 4) * mm});
            skLineSegment(sketch, "E34.1.0.18", {"start": v(-1.45, 4.55) * mm, "end": v(-2.55, 4.55) * mm});
            skLineSegment(sketch, "E34.1.0.19", {"start": v(-1.45, 3.45) * mm, "end": v(-1.45, 4.55) * mm});
            skLineSegment(sketch, "E34.1.0.20", {"start": v(-2.55, 3.45) * mm, "end": v(-2.55, 4.55) * mm});
            skPoint(sketch, "E34.2.0.0", {"position": v(-4, -6) * mm});
            skLineSegment(sketch, "E34.2.0.1", {"start": v(-3.45, -4.55) * mm, "end": v(-4.55, -4.55) * mm});
            skLineSegment(sketch, "E34.2.0.2", {"start": v(-3.45, -4.55) * mm, "end": v(-3.45, -3.45) * mm});
            skLineSegment(sketch, "E34.2.0.3", {"start": v(-3.45, -3.45) * mm, "end": v(-4.55, -3.45) * mm});
            skPoint(sketch, "E34.2.0.4", {"position": v(-4, -4) * mm});
            skLineSegment(sketch, "E34.2.0.5", {"start": v(-4.55, -4.55) * mm, "end": v(-4.55, -3.45) * mm});
            skLineSegment(sketch, "E34.2.0.6", {"start": v(-4.55, -6.55) * mm, "end": v(-4.55, -5.45) * mm});
            skPoint(sketch, "E34.2.0.7", {"position": v(-3.45, -6) * mm});
            skLineSegment(sketch, "E34.2.0.8", {"start": v(-3.45, -6.55) * mm, "end": v(-3.45, -5.45) * mm});
            skLineSegment(sketch, "E34.2.0.9", {"start": v(-3.45, -6.55) * mm, "end": v(-4.55, -6.55) * mm});
            skLineSegment(sketch, "E34.2.0.10", {"start": v(-3.45, -5.45) * mm, "end": v(-4.55, -5.45) * mm});
            skPoint(sketch, "E34.2.0.11", {"position": v(-4, 6) * mm});
            skLineSegment(sketch, "E34.2.0.12", {"start": v(-3.45, 5.45) * mm, "end": v(-4.55, 5.45) * mm});
            skLineSegment(sketch, "E34.2.0.13", {"start": v(-3.45, 6.55) * mm, "end": v(-4.55, 6.55) * mm});
            skLineSegment(sketch, "E34.2.0.14", {"start": v(-4.55, 5.45) * mm, "end": v(-4.55, 6.55) * mm});
            skLineSegment(sketch, "E34.2.0.15", {"start": v(-3.45, 5.45) * mm, "end": v(-3.45, 6.55) * mm});
            skLineSegment(sketch, "E34.2.0.16", {"start": v(-3.45, 3.45) * mm, "end": v(-4.55, 3.45) * mm});
            skPoint(sketch, "E34.2.0.17", {"position": v(-4, 4) * mm});
            skLineSegment(sketch, "E34.2.0.18", {"start": v(-3.45, 4.55) * mm, "end": v(-4.55, 4.55) * mm});
            skLineSegment(sketch, "E34.2.0.19", {"start": v(-3.45, 3.45) * mm, "end": v(-3.45, 4.55) * mm});
            skLineSegment(sketch, "E34.2.0.20", {"start": v(-4.55, 3.45) * mm, "end": v(-4.55, 4.55) * mm});
            skPoint(sketch, "E34.3.0.0", {"position": v(-6, -6) * mm});
            skLineSegment(sketch, "E34.3.0.1", {"start": v(-5.45, -4.55) * mm, "end": v(-6.55, -4.55) * mm});
            skLineSegment(sketch, "E34.3.0.2", {"start": v(-5.45, -4.55) * mm, "end": v(-5.45, -3.45) * mm});
            skLineSegment(sketch, "E34.3.0.3", {"start": v(-5.45, -3.45) * mm, "end": v(-6.55, -3.45) * mm});
            skPoint(sketch, "E34.3.0.4", {"position": v(-6, -4) * mm});
            skLineSegment(sketch, "E34.3.0.5", {"start": v(-6.55, -4.55) * mm, "end": v(-6.55, -3.45) * mm});
            skLineSegment(sketch, "E34.3.0.6", {"start": v(-6.55, -6.55) * mm, "end": v(-6.55, -5.45) * mm});
            skPoint(sketch, "E34.3.0.7", {"position": v(-5.45, -6) * mm});
            skLineSegment(sketch, "E34.3.0.8", {"start": v(-5.45, -6.55) * mm, "end": v(-5.45, -5.45) * mm});
            skLineSegment(sketch, "E34.3.0.9", {"start": v(-5.45, -6.55) * mm, "end": v(-6.55, -6.55) * mm});
            skLineSegment(sketch, "E34.3.0.10", {"start": v(-5.45, -5.45) * mm, "end": v(-6.55, -5.45) * mm});
            skPoint(sketch, "E34.3.0.11", {"position": v(-6, 6) * mm});
            skLineSegment(sketch, "E34.3.0.12", {"start": v(-5.45, 5.45) * mm, "end": v(-6.55, 5.45) * mm});
            skLineSegment(sketch, "E34.3.0.13", {"start": v(-5.45, 6.55) * mm, "end": v(-6.55, 6.55) * mm});
            skLineSegment(sketch, "E34.3.0.14", {"start": v(-6.55, 5.45) * mm, "end": v(-6.55, 6.55) * mm});
            skLineSegment(sketch, "E34.3.0.15", {"start": v(-5.45, 5.45) * mm, "end": v(-5.45, 6.55) * mm});
            skLineSegment(sketch, "E34.3.0.16", {"start": v(-5.45, 3.45) * mm, "end": v(-6.55, 3.45) * mm});
            skPoint(sketch, "E34.3.0.17", {"position": v(-6, 4) * mm});
            skLineSegment(sketch, "E34.3.0.18", {"start": v(-5.45, 4.55) * mm, "end": v(-6.55, 4.55) * mm});
            skLineSegment(sketch, "E34.3.0.19", {"start": v(-5.45, 3.45) * mm, "end": v(-5.45, 4.55) * mm});
            skLineSegment(sketch, "E34.3.0.20", {"start": v(-6.55, 3.45) * mm, "end": v(-6.55, 4.55) * mm});
            skLineSegment(sketch, "E34.direction1", {"start": v(-0.55, -6.55) * mm, "end": v(-2.55, -6.55) * mm, "construction": true});
            skLineSegment(sketch, "E35.bottom", {"start": v(-8.55, -0.55) * mm, "end": v(-7.45, -0.55) * mm});
            skLineSegment(sketch, "E35.top", {"start": v(-8.55, 0.55) * mm, "end": v(-7.45, 0.55) * mm});
            skLineSegment(sketch, "E35.left", {"start": v(-8.55, -0.55) * mm, "end": v(-8.55, 0.55) * mm});
            skLineSegment(sketch, "E35.right", {"start": v(-7.45, -0.55) * mm, "end": v(-7.45, 0.55) * mm});
            skPoint(sketch, "E35.middle", {"position": v(-8, 0) * mm});
            skLineSegment(sketch, "E36.bottom", {"start": v(-10.55, -0.55) * mm, "end": v(-9.45, -0.55) * mm});
            skLineSegment(sketch, "E36.top", {"start": v(-10.55, 0.55) * mm, "end": v(-9.45, 0.55) * mm});
            skLineSegment(sketch, "E36.left", {"start": v(-10.55, -0.55) * mm, "end": v(-10.55, 0.55) * mm});
            skLineSegment(sketch, "E36.right", {"start": v(-9.45, -0.55) * mm, "end": v(-9.45, 0.55) * mm});
            skPoint(sketch, "E36.middle", {"position": v(-10, 0) * mm});
            skLineSegment(sketch, "E37.bottom", {"start": v(8.55, -0.55) * mm, "end": v(7.45, -0.55) * mm});
            skLineSegment(sketch, "E37.top", {"start": v(8.55, 0.55) * mm, "end": v(7.45, 0.55) * mm});
            skLineSegment(sketch, "E37.left", {"start": v(8.55, -0.55) * mm, "end": v(8.55, 0.55) * mm});
            skLineSegment(sketch, "E37.right", {"start": v(7.45, -0.55) * mm, "end": v(7.45, 0.55) * mm});
            skPoint(sketch, "E37.middle", {"position": v(8, 0) * mm});
            skLineSegment(sketch, "E38.bottom", {"start": v(10.55, -0.55) * mm, "end": v(9.45, -0.55) * mm});
            skLineSegment(sketch, "E38.top", {"start": v(10.55, 0.55) * mm, "end": v(9.45, 0.55) * mm});
            skLineSegment(sketch, "E38.left", {"start": v(10.55, -0.55) * mm, "end": v(10.55, 0.55) * mm});
            skLineSegment(sketch, "E38.right", {"start": v(9.45, -0.55) * mm, "end": v(9.45, 0.55) * mm});
            skPoint(sketch, "E38.middle", {"position": v(10, 0) * mm});
            skPoint(sketch, "E39.0.1.0", {"position": v(-8, 2) * mm});
            skLineSegment(sketch, "E39.0.1.1", {"start": v(-10.55, 1.45) * mm, "end": v(-9.45, 1.45) * mm});
            skLineSegment(sketch, "E39.0.1.2", {"start": v(-10.55, 2.55) * mm, "end": v(-9.45, 2.55) * mm});
            skLineSegment(sketch, "E39.0.1.3", {"start": v(-8.55, 1.45) * mm, "end": v(-7.45, 1.45) * mm});
            skLineSegment(sketch, "E39.0.1.4", {"start": v(-7.45, 1.45) * mm, "end": v(-7.45, 2.55) * mm});
            skLineSegment(sketch, "E39.0.1.5", {"start": v(-8.55, 1.45) * mm, "end": v(-8.55, 2.55) * mm});
            skLineSegment(sketch, "E39.0.1.6", {"start": v(-8.55, 2.55) * mm, "end": v(-7.45, 2.55) * mm});
            skPoint(sketch, "E39.0.1.7", {"position": v(-10, 2) * mm});
            skLineSegment(sketch, "E39.0.1.8", {"start": v(-9.45, 1.45) * mm, "end": v(-9.45, 2.55) * mm});
            skLineSegment(sketch, "E39.0.1.9", {"start": v(-10.55, 1.45) * mm, "end": v(-10.55, 2.55) * mm});
            skLineSegment(sketch, "E39.0.1.10", {"start": v(8.55, 1.45) * mm, "end": v(7.45, 1.45) * mm});
            skLineSegment(sketch, "E39.0.1.11", {"start": v(8.55, 2.55) * mm, "end": v(7.45, 2.55) * mm});
            skPoint(sketch, "E39.0.1.12", {"position": v(8, 2) * mm});
            skLineSegment(sketch, "E39.0.1.13", {"start": v(7.45, 1.45) * mm, "end": v(7.45, 2.55) * mm});
            skLineSegment(sketch, "E39.0.1.14", {"start": v(10.55, 1.45) * mm, "end": v(9.45, 1.45) * mm});
            skPoint(sketch, "E39.0.1.15", {"position": v(10, 2) * mm});
            skLineSegment(sketch, "E39.0.1.16", {"start": v(10.55, 2.55) * mm, "end": v(9.45, 2.55) * mm});
            skLineSegment(sketch, "E39.0.1.17", {"start": v(10.55, 1.45) * mm, "end": v(10.55, 2.55) * mm});
            skLineSegment(sketch, "E39.0.1.18", {"start": v(9.45, 1.45) * mm, "end": v(9.45, 2.55) * mm});
            skLineSegment(sketch, "E39.0.1.19", {"start": v(8.55, 1.45) * mm, "end": v(8.55, 2.55) * mm});
            skLineSegment(sketch, "E39.direction1", {"start": v(-10.55, -0.55) * mm, "end": v(14.45, -0.55) * mm, "construction": true});
            skLineSegment(sketch, "E39.direction2", {"start": v(-10.55, -0.55) * mm, "end": v(-10.55, 1.45) * mm, "construction": true});
            skLineSegment(sketch, "E40.0.1.0", {"start": v(-9.45, -2.55) * mm, "end": v(-9.45, -1.45) * mm});
            skLineSegment(sketch, "E40.0.1.1", {"start": v(-10.55, -2.55) * mm, "end": v(-10.55, -1.45) * mm});
            skLineSegment(sketch, "E40.0.1.2", {"start": v(-10.55, -1.45) * mm, "end": v(-9.45, -1.45) * mm});
            skLineSegment(sketch, "E40.0.1.3", {"start": v(-10.55, -2.55) * mm, "end": v(-9.45, -2.55) * mm});
            skLineSegment(sketch, "E40.0.1.4", {"start": v(-7.45, -2.55) * mm, "end": v(-7.45, -1.45) * mm});
            skLineSegment(sketch, "E40.0.1.5", {"start": v(-8.55, -2.55) * mm, "end": v(-7.45, -2.55) * mm});
            skLineSegment(sketch, "E40.0.1.6", {"start": v(-8.55, -2.55) * mm, "end": v(-8.55, -1.45) * mm});
            skLineSegment(sketch, "E40.0.1.7", {"start": v(-8.55, -1.45) * mm, "end": v(-7.45, -1.45) * mm});
            skPoint(sketch, "E40.0.1.8", {"position": v(-8, -2) * mm});
            skPoint(sketch, "E40.0.1.9", {"position": v(-10, -2) * mm});
            skLineSegment(sketch, "E40.0.1.10", {"start": v(8.55, -1.45) * mm, "end": v(7.45, -1.45) * mm});
            skLineSegment(sketch, "E40.0.1.11", {"start": v(8.55, -2.55) * mm, "end": v(7.45, -2.55) * mm});
            skLineSegment(sketch, "E40.0.1.12", {"start": v(10.55, -2.55) * mm, "end": v(9.45, -2.55) * mm});
            skLineSegment(sketch, "E40.0.1.13", {"start": v(7.45, -2.55) * mm, "end": v(7.45, -1.45) * mm});
            skLineSegment(sketch, "E40.0.1.14", {"start": v(10.55, -1.45) * mm, "end": v(9.45, -1.45) * mm});
            skLineSegment(sketch, "E40.0.1.15", {"start": v(10.55, -2.55) * mm, "end": v(10.55, -1.45) * mm});
            skLineSegment(sketch, "E40.0.1.16", {"start": v(9.45, -2.55) * mm, "end": v(9.45, -1.45) * mm});
            skPoint(sketch, "E40.0.1.17", {"position": v(8, -2) * mm});
            skPoint(sketch, "E40.0.1.18", {"position": v(10, -2) * mm});
            skLineSegment(sketch, "E40.0.1.19", {"start": v(8.55, -2.55) * mm, "end": v(8.55, -1.45) * mm});
            skLineSegment(sketch, "E40.direction2", {"start": v(-10.55, -0.55) * mm, "end": v(-10.55, -2.55) * mm, "construction": true});
            skLineSegment(sketch, "E41.bottom", {"start": v(13.5, 7.4) * mm, "end": v(12, 7.4) * mm});
            skLineSegment(sketch, "E41.top", {"start": v(13.5, 8.2) * mm, "end": v(12, 8.2) * mm});
            skLineSegment(sketch, "E41.left", {"start": v(13.5, 7.4) * mm, "end": v(13.5, 8.2) * mm});
            skLineSegment(sketch, "E41.right", {"start": v(12, 7.4) * mm, "end": v(12, 8.2) * mm});
            skPoint(sketch, "E41.middle", {"position": v(12.75, 7.8) * mm});
            skLineSegment(sketch, "E42.0.1.0", {"start": v(13.5, 6.2) * mm, "end": v(13.5, 7) * mm});
            skLineSegment(sketch, "E42.0.1.1", {"start": v(12, 6.2) * mm, "end": v(12, 7) * mm});
            skLineSegment(sketch, "E42.0.1.2", {"start": v(13.5, 7) * mm, "end": v(12, 7) * mm});
            skLineSegment(sketch, "E42.0.1.3", {"start": v(13.5, 6.2) * mm, "end": v(12, 6.2) * mm});
            skPoint(sketch, "E42.0.1.4", {"position": v(12.75, 6.6) * mm});
            skLineSegment(sketch, "E42.0.2.0", {"start": v(13.5, 5) * mm, "end": v(13.5, 5.8) * mm});
            skLineSegment(sketch, "E42.0.2.1", {"start": v(12, 5) * mm, "end": v(12, 5.8) * mm});
            skLineSegment(sketch, "E42.0.2.2", {"start": v(13.5, 5.8) * mm, "end": v(12, 5.8) * mm});
            skLineSegment(sketch, "E42.0.2.3", {"start": v(13.5, 5) * mm, "end": v(12, 5) * mm});
            skPoint(sketch, "E42.0.2.4", {"position": v(12.75, 5.4) * mm});
            skLineSegment(sketch, "E42.0.3.0", {"start": v(13.5, 3.8) * mm, "end": v(13.5, 4.6) * mm});
            skLineSegment(sketch, "E42.0.3.1", {"start": v(12, 3.8) * mm, "end": v(12, 4.6) * mm});
            skLineSegment(sketch, "E42.0.3.2", {"start": v(13.5, 4.6) * mm, "end": v(12, 4.6) * mm});
            skLineSegment(sketch, "E42.0.3.3", {"start": v(13.5, 3.8) * mm, "end": v(12, 3.8) * mm});
            skPoint(sketch, "E42.0.3.4", {"position": v(12.75, 4.2) * mm});
            skLineSegment(sketch, "E42.0.4.0", {"start": v(13.5, 2.6) * mm, "end": v(13.5, 3.4) * mm});
            skLineSegment(sketch, "E42.0.4.1", {"start": v(12, 2.6) * mm, "end": v(12, 3.4) * mm});
            skLineSegment(sketch, "E42.0.4.2", {"start": v(13.5, 3.4) * mm, "end": v(12, 3.4) * mm});
            skLineSegment(sketch, "E42.0.4.3", {"start": v(13.5, 2.6) * mm, "end": v(12, 2.6) * mm});
            skPoint(sketch, "E42.0.4.4", {"position": v(12.75, 3) * mm});
            skLineSegment(sketch, "E42.0.5.0", {"start": v(13.5, 1.4) * mm, "end": v(13.5, 2.2) * mm});
            skLineSegment(sketch, "E42.0.5.1", {"start": v(12, 1.4) * mm, "end": v(12, 2.2) * mm});
            skLineSegment(sketch, "E42.0.5.2", {"start": v(13.5, 2.2) * mm, "end": v(12, 2.2) * mm});
            skLineSegment(sketch, "E42.0.5.3", {"start": v(13.5, 1.4) * mm, "end": v(12, 1.4) * mm});
            skPoint(sketch, "E42.0.5.4", {"position": v(12.75, 1.8) * mm});
            skLineSegment(sketch, "E42.0.6.0", {"start": v(13.5, 0.2) * mm, "end": v(13.5, 1) * mm});
            skLineSegment(sketch, "E42.0.6.1", {"start": v(12, 0.2) * mm, "end": v(12, 1) * mm});
            skLineSegment(sketch, "E42.0.6.2", {"start": v(13.5, 1) * mm, "end": v(12, 1) * mm});
            skLineSegment(sketch, "E42.0.6.3", {"start": v(13.5, 0.2) * mm, "end": v(12, 0.2) * mm});
            skPoint(sketch, "E42.0.6.4", {"position": v(12.75, 0.6) * mm});
            skLineSegment(sketch, "E42.0.7.0", {"start": v(13.5, -1) * mm, "end": v(13.5, -0.2) * mm});
            skLineSegment(sketch, "E42.0.7.1", {"start": v(12, -1) * mm, "end": v(12, -0.2) * mm});
            skLineSegment(sketch, "E42.0.7.2", {"start": v(13.5, -0.2) * mm, "end": v(12, -0.2) * mm});
            skLineSegment(sketch, "E42.0.7.3", {"start": v(13.5, -1) * mm, "end": v(12, -1) * mm});
            skPoint(sketch, "E42.0.7.4", {"position": v(12.75, -0.6) * mm});
            skLineSegment(sketch, "E42.0.8.0", {"start": v(13.5, -2.2) * mm, "end": v(13.5, -1.4) * mm});
            skLineSegment(sketch, "E42.0.8.1", {"start": v(12, -2.2) * mm, "end": v(12, -1.4) * mm});
            skLineSegment(sketch, "E42.0.8.2", {"start": v(13.5, -1.4) * mm, "end": v(12, -1.4) * mm});
            skLineSegment(sketch, "E42.0.8.3", {"start": v(13.5, -2.2) * mm, "end": v(12, -2.2) * mm});
            skPoint(sketch, "E42.0.8.4", {"position": v(12.75, -1.8) * mm});
            skLineSegment(sketch, "E42.0.9.0", {"start": v(13.5, -3.4) * mm, "end": v(13.5, -2.6) * mm});
            skLineSegment(sketch, "E42.0.9.1", {"start": v(12, -3.4) * mm, "end": v(12, -2.6) * mm});
            skLineSegment(sketch, "E42.0.9.2", {"start": v(13.5, -2.6) * mm, "end": v(12, -2.6) * mm});
            skLineSegment(sketch, "E42.0.9.3", {"start": v(13.5, -3.4) * mm, "end": v(12, -3.4) * mm});
            skPoint(sketch, "E42.0.9.4", {"position": v(12.75, -3) * mm});
            skLineSegment(sketch, "E42.0.10.0", {"start": v(13.5, -4.6) * mm, "end": v(13.5, -3.8) * mm});
            skLineSegment(sketch, "E42.0.10.1", {"start": v(12, -4.6) * mm, "end": v(12, -3.8) * mm});
            skLineSegment(sketch, "E42.0.10.2", {"start": v(13.5, -3.8) * mm, "end": v(12, -3.8) * mm});
            skLineSegment(sketch, "E42.0.10.3", {"start": v(13.5, -4.6) * mm, "end": v(12, -4.6) * mm});
            skPoint(sketch, "E42.0.10.4", {"position": v(12.75, -4.2) * mm});
            skLineSegment(sketch, "E42.0.11.0", {"start": v(13.5, -5.8) * mm, "end": v(13.5, -5) * mm});
            skLineSegment(sketch, "E42.0.11.1", {"start": v(12, -5.8) * mm, "end": v(12, -5) * mm});
            skLineSegment(sketch, "E42.0.11.2", {"start": v(13.5, -5) * mm, "end": v(12, -5) * mm});
            skLineSegment(sketch, "E42.0.11.3", {"start": v(13.5, -5.8) * mm, "end": v(12, -5.8) * mm});
            skPoint(sketch, "E42.0.11.4", {"position": v(12.75, -5.4) * mm});
            skLineSegment(sketch, "E42.0.12.0", {"start": v(13.5, -7) * mm, "end": v(13.5, -6.2) * mm});
            skLineSegment(sketch, "E42.0.12.1", {"start": v(12, -7) * mm, "end": v(12, -6.2) * mm});
            skLineSegment(sketch, "E42.0.12.2", {"start": v(13.5, -6.2) * mm, "end": v(12, -6.2) * mm});
            skLineSegment(sketch, "E42.0.12.3", {"start": v(13.5, -7) * mm, "end": v(12, -7) * mm});
            skPoint(sketch, "E42.0.12.4", {"position": v(12.75, -6.6) * mm});
            skLineSegment(sketch, "E42.0.13.0", {"start": v(13.5, -8.2) * mm, "end": v(13.5, -7.4) * mm});
            skLineSegment(sketch, "E42.0.13.1", {"start": v(12, -8.2) * mm, "end": v(12, -7.4) * mm});
            skLineSegment(sketch, "E42.0.13.2", {"start": v(13.5, -7.4) * mm, "end": v(12, -7.4) * mm});
            skLineSegment(sketch, "E42.0.13.3", {"start": v(13.5, -8.2) * mm, "end": v(12, -8.2) * mm});
            skPoint(sketch, "E42.0.13.4", {"position": v(12.75, -7.8) * mm});
            skLineSegment(sketch, "E42.direction1", {"start": v(12, 7.4) * mm, "end": v(37, 7.4) * mm, "construction": true});
            skLineSegment(sketch, "E42.direction2", {"start": v(12, 7.4) * mm, "end": v(12, 6.2) * mm, "construction": true});
            skLineSegment(sketch, "E43.bottom", {"start": v(-12, 0.2) * mm, "end": v(-13.5, 0.2) * mm});
            skLineSegment(sketch, "E43.top", {"start": v(-12, 1) * mm, "end": v(-13.5, 1) * mm});
            skLineSegment(sketch, "E43.left", {"start": v(-12, 0.2) * mm, "end": v(-12, 1) * mm});
            skLineSegment(sketch, "E43.right", {"start": v(-13.5, 0.2) * mm, "end": v(-13.5, 1) * mm});
            skPoint(sketch, "E43.middle", {"position": v(-12.75, 0.6) * mm});
            skLineSegment(sketch, "E44.bottom", {"start": v(-12, 1.55) * mm, "end": v(-13.5, 1.55) * mm});
            skLineSegment(sketch, "E44.top", {"start": v(-12, 2.35) * mm, "end": v(-13.5, 2.35) * mm});
            skLineSegment(sketch, "E44.left", {"start": v(-12, 1.55) * mm, "end": v(-12, 2.35) * mm});
            skLineSegment(sketch, "E44.right", {"start": v(-13.5, 1.55) * mm, "end": v(-13.5, 2.35) * mm});
            skPoint(sketch, "E44.middle", {"position": v(-12.75, 1.95) * mm});
            skLineSegment(sketch, "E45.0.1.0", {"start": v(-12, 2.75) * mm, "end": v(-13.5, 2.75) * mm});
            skPoint(sketch, "E45.0.1.1", {"position": v(-12.75, 3.15) * mm});
            skLineSegment(sketch, "E45.0.1.2", {"start": v(-12, 2.75) * mm, "end": v(-12, 3.55) * mm});
            skLineSegment(sketch, "E45.0.1.3", {"start": v(-12, 3.55) * mm, "end": v(-13.5, 3.55) * mm});
            skLineSegment(sketch, "E45.0.1.4", {"start": v(-13.5, 2.75) * mm, "end": v(-13.5, 3.55) * mm});
            skLineSegment(sketch, "E45.0.2.0", {"start": v(-12, 3.95) * mm, "end": v(-13.5, 3.95) * mm});
            skPoint(sketch, "E45.0.2.1", {"position": v(-12.75, 4.35) * mm});
            skLineSegment(sketch, "E45.0.2.2", {"start": v(-12, 3.95) * mm, "end": v(-12, 4.75) * mm});
            skLineSegment(sketch, "E45.0.2.3", {"start": v(-12, 4.75) * mm, "end": v(-13.5, 4.75) * mm});
            skLineSegment(sketch, "E45.0.2.4", {"start": v(-13.5, 3.95) * mm, "end": v(-13.5, 4.75) * mm});
            skLineSegment(sketch, "E45.0.3.0", {"start": v(-12, 5.15) * mm, "end": v(-13.5, 5.15) * mm});
            skPoint(sketch, "E45.0.3.1", {"position": v(-12.75, 5.55) * mm});
            skLineSegment(sketch, "E45.0.3.2", {"start": v(-12, 5.15) * mm, "end": v(-12, 5.95) * mm});
            skLineSegment(sketch, "E45.0.3.3", {"start": v(-12, 5.95) * mm, "end": v(-13.5, 5.95) * mm});
            skLineSegment(sketch, "E45.0.3.4", {"start": v(-13.5, 5.15) * mm, "end": v(-13.5, 5.95) * mm});
            skLineSegment(sketch, "E45.0.4.0", {"start": v(-12, 6.35) * mm, "end": v(-13.5, 6.35) * mm});
            skPoint(sketch, "E45.0.4.1", {"position": v(-12.75, 6.75) * mm});
            skLineSegment(sketch, "E45.0.4.2", {"start": v(-12, 6.35) * mm, "end": v(-12, 7.15) * mm});
            skLineSegment(sketch, "E45.0.4.3", {"start": v(-12, 7.15) * mm, "end": v(-13.5, 7.15) * mm});
            skLineSegment(sketch, "E45.0.4.4", {"start": v(-13.5, 6.35) * mm, "end": v(-13.5, 7.15) * mm});
            skLineSegment(sketch, "E45.0.5.0", {"start": v(-12, 7.55) * mm, "end": v(-13.5, 7.55) * mm});
            skPoint(sketch, "E45.0.5.1", {"position": v(-12.75, 7.95) * mm});
            skLineSegment(sketch, "E45.0.5.2", {"start": v(-12, 7.55) * mm, "end": v(-12, 8.35) * mm});
            skLineSegment(sketch, "E45.0.5.3", {"start": v(-12, 8.35) * mm, "end": v(-13.5, 8.35) * mm});
            skLineSegment(sketch, "E45.0.5.4", {"start": v(-13.5, 7.55) * mm, "end": v(-13.5, 8.35) * mm});
            skLineSegment(sketch, "E45.direction1", {"start": v(-13.5, 1.55) * mm, "end": v(-38.11, 1.55) * mm, "construction": true});
            skLineSegment(sketch, "E45.direction2", {"start": v(-13.5, 1.55) * mm, "end": v(-13.5, 2.75) * mm, "construction": true});
            skLineSegment(sketch, "E46.bottom", {"start": v(-13.5, -1.15) * mm, "end": v(-12, -1.15) * mm});
            skLineSegment(sketch, "E46.top", {"start": v(-13.5, -0.35) * mm, "end": v(-12, -0.35) * mm});
            skLineSegment(sketch, "E46.left", {"start": v(-13.5, -1.15) * mm, "end": v(-13.5, -0.35) * mm});
            skLineSegment(sketch, "E46.right", {"start": v(-12, -1.15) * mm, "end": v(-12, -0.35) * mm});
            skPoint(sketch, "E46.middle", {"position": v(-12.75, -0.75) * mm});
            skPoint(sketch, "E47.0.1.0", {"position": v(-12.75, -1.95) * mm});
            skLineSegment(sketch, "E47.0.1.1", {"start": v(-13.5, -2.35) * mm, "end": v(-13.5, -1.55) * mm});
            skLineSegment(sketch, "E47.0.1.2", {"start": v(-13.5, -2.35) * mm, "end": v(-12, -2.35) * mm});
            skLineSegment(sketch, "E47.0.1.3", {"start": v(-13.5, -1.55) * mm, "end": v(-12, -1.55) * mm});
            skLineSegment(sketch, "E47.0.1.4", {"start": v(-12, -2.35) * mm, "end": v(-12, -1.55) * mm});
            skPoint(sketch, "E47.0.2.0", {"position": v(-12.75, -3.15) * mm});
            skLineSegment(sketch, "E47.0.2.1", {"start": v(-13.5, -3.55) * mm, "end": v(-13.5, -2.75) * mm});
            skLineSegment(sketch, "E47.0.2.2", {"start": v(-13.5, -3.55) * mm, "end": v(-12, -3.55) * mm});
            skLineSegment(sketch, "E47.0.2.3", {"start": v(-13.5, -2.75) * mm, "end": v(-12, -2.75) * mm});
            skLineSegment(sketch, "E47.0.2.4", {"start": v(-12, -3.55) * mm, "end": v(-12, -2.75) * mm});
            skPoint(sketch, "E47.0.3.0", {"position": v(-12.75, -4.35) * mm});
            skLineSegment(sketch, "E47.0.3.1", {"start": v(-13.5, -4.75) * mm, "end": v(-13.5, -3.95) * mm});
            skLineSegment(sketch, "E47.0.3.2", {"start": v(-13.5, -4.75) * mm, "end": v(-12, -4.75) * mm});
            skLineSegment(sketch, "E47.0.3.3", {"start": v(-13.5, -3.95) * mm, "end": v(-12, -3.95) * mm});
            skLineSegment(sketch, "E47.0.3.4", {"start": v(-12, -4.75) * mm, "end": v(-12, -3.95) * mm});
            skPoint(sketch, "E47.0.4.0", {"position": v(-12.75, -5.55) * mm});
            skLineSegment(sketch, "E47.0.4.1", {"start": v(-13.5, -5.95) * mm, "end": v(-13.5, -5.15) * mm});
            skLineSegment(sketch, "E47.0.4.2", {"start": v(-13.5, -5.95) * mm, "end": v(-12, -5.95) * mm});
            skLineSegment(sketch, "E47.0.4.3", {"start": v(-13.5, -5.15) * mm, "end": v(-12, -5.15) * mm});
            skLineSegment(sketch, "E47.0.4.4", {"start": v(-12, -5.95) * mm, "end": v(-12, -5.15) * mm});
            skPoint(sketch, "E47.0.5.0", {"position": v(-12.75, -6.75) * mm});
            skLineSegment(sketch, "E47.0.5.1", {"start": v(-13.5, -7.15) * mm, "end": v(-13.5, -6.35) * mm});
            skLineSegment(sketch, "E47.0.5.2", {"start": v(-13.5, -7.15) * mm, "end": v(-12, -7.15) * mm});
            skLineSegment(sketch, "E47.0.5.3", {"start": v(-13.5, -6.35) * mm, "end": v(-12, -6.35) * mm});
            skLineSegment(sketch, "E47.0.5.4", {"start": v(-12, -7.15) * mm, "end": v(-12, -6.35) * mm});
            skPoint(sketch, "E47.0.6.0", {"position": v(-12.75, -7.95) * mm});
            skLineSegment(sketch, "E47.0.6.1", {"start": v(-13.5, -8.35) * mm, "end": v(-13.5, -7.55) * mm});
            skLineSegment(sketch, "E47.0.6.2", {"start": v(-13.5, -8.35) * mm, "end": v(-12, -8.35) * mm});
            skLineSegment(sketch, "E47.0.6.3", {"start": v(-13.5, -7.55) * mm, "end": v(-12, -7.55) * mm});
            skLineSegment(sketch, "E47.0.6.4", {"start": v(-12, -8.35) * mm, "end": v(-12, -7.55) * mm});
            skLineSegment(sketch, "E47.direction1", {"start": v(-13.5, -1.15) * mm, "end": v(11.5, -1.15) * mm, "construction": true});
            skLineSegment(sketch, "E47.direction2", {"start": v(-13.5, -1.15) * mm, "end": v(-13.5, -2.35) * mm, "construction": true});
            skLineSegment(sketch, "E48", {"start": v(0, 0) * mm, "end": v(-12.75, 0) * mm});
            skPoint(sketch, "E48.endSnap0", {"position": v(-12.75, -0.35) * mm});
            skLineSegment(sketch, "E49", {"start": v(-12.75, 0) * mm, "end": v(-12.75, 0.6) * mm});
            skPoint(sketch, "E50.endSnap0", {"position": v(-12.75, 1) * mm});
            skLineSegment(sketch, "E51", {"start": v(-12.75, 0.6) * mm, "end": v(-12.75, -0.75) * mm});
            skSolve(sketch);
        }
        {
            var Q0;
            Q0 = qSketchRegion(id + "F6", true);
            extrude(context, id + "F7", {"entities" : qUnion([Q0]), "operationType" : NewBodyOperationType.REMOVE, "oppositeDirection" : true, "depth" : 0.05 * mm});
        }
        {
            var Q0;
            Q0=makeQuery(id+"F7.boolean.opBoolean","COPY",FACE,{"derivedFrom":makeQuery(id+"F7.opExtrude","CAP_FACE",FACE,{"disambiguationData":[OSD([sQuery(id+"F6.wireOp",EDGE,"E45.0.5.0"),sQuery(id+"F6.wireOp",EDGE,"E45.0.5.2"),sQuery(id+"F6.wireOp",EDGE,"E45.0.5.3"),sQuery(id+"F6.wireOp",EDGE,"E45.0.5.4")])],"isStart":false})});
            var Q1;
            Q1=makeQuery(id+"F7.boolean.opBoolean","COPY",FACE,{"derivedFrom":makeQuery(id+"F7.opExtrude","CAP_FACE",FACE,{"disambiguationData":[OSD([sQuery(id+"F6.wireOp",EDGE,"E45.0.4.0"),sQuery(id+"F6.wireOp",EDGE,"E45.0.4.2"),sQuery(id+"F6.wireOp",EDGE,"E45.0.4.3"),sQuery(id+"F6.wireOp",EDGE,"E45.0.4.4")])],"isStart":false})});
            var Q2;
            Q2=makeQuery(id+"F7.boolean.opBoolean","COPY",FACE,{"derivedFrom":makeQuery(id+"F7.opExtrude","CAP_FACE",FACE,{"disambiguationData":[OSD([sQuery(id+"F6.wireOp",EDGE,"E45.0.3.0"),sQuery(id+"F6.wireOp",EDGE,"E45.0.3.2"),sQuery(id+"F6.wireOp",EDGE,"E45.0.3.3"),sQuery(id+"F6.wireOp",EDGE,"E45.0.3.4")])],"isStart":false})});
            var Q3;
            Q3=makeQuery(id+"F7.boolean.opBoolean","COPY",FACE,{"derivedFrom":makeQuery(id+"F7.opExtrude","CAP_FACE",FACE,{"disambiguationData":[OSD([sQuery(id+"F6.wireOp",EDGE,"E45.0.2.0"),sQuery(id+"F6.wireOp",EDGE,"E45.0.2.2"),sQuery(id+"F6.wireOp",EDGE,"E45.0.2.3"),sQuery(id+"F6.wireOp",EDGE,"E45.0.2.4")])],"isStart":false})});
            var Q4;
            Q4=makeQuery(id+"F7.boolean.opBoolean","COPY",FACE,{"derivedFrom":makeQuery(id+"F7.opExtrude","CAP_FACE",FACE,{"disambiguationData":[OSD([sQuery(id+"F6.wireOp",EDGE,"E45.0.1.0"),sQuery(id+"F6.wireOp",EDGE,"E45.0.1.2"),sQuery(id+"F6.wireOp",EDGE,"E45.0.1.3"),sQuery(id+"F6.wireOp",EDGE,"E45.0.1.4")])],"isStart":false})});
            var Q5;
            Q5=makeQuery(id+"F7.boolean.opBoolean","COPY",FACE,{"derivedFrom":makeQuery(id+"F7.opExtrude","CAP_FACE",FACE,{"disambiguationData":[OSD([sQuery(id+"F6.wireOp",EDGE,"E44.bottom"),sQuery(id+"F6.wireOp",EDGE,"E44.top"),sQuery(id+"F6.wireOp",EDGE,"E44.left"),sQuery(id+"F6.wireOp",EDGE,"E44.right")])],"isStart":false})});
            var Q6;
            Q6=makeQuery(id+"F7.boolean.opBoolean","COPY",FACE,{"derivedFrom":makeQuery(id+"F7.opExtrude","CAP_FACE",FACE,{"disambiguationData":[OSD([sQuery(id+"F6.wireOp",EDGE,"E43.bottom"),sQuery(id+"F6.wireOp",EDGE,"E43.top"),sQuery(id+"F6.wireOp",EDGE,"E43.left"),sQuery(id+"F6.wireOp",EDGE,"E43.right")])],"isStart":false})});
            var Q7;
            Q7=makeQuery(id+"F7.boolean.opBoolean","COPY",FACE,{"derivedFrom":makeQuery(id+"F7.opExtrude","CAP_FACE",FACE,{"disambiguationData":[OSD([sQuery(id+"F6.wireOp",EDGE,"E46.bottom"),sQuery(id+"F6.wireOp",EDGE,"E46.top"),sQuery(id+"F6.wireOp",EDGE,"E46.left"),sQuery(id+"F6.wireOp",EDGE,"E46.right")])],"isStart":false})});
            var Q8;
            Q8=makeQuery(id+"F7.boolean.opBoolean","COPY",FACE,{"derivedFrom":makeQuery(id+"F7.opExtrude","CAP_FACE",FACE,{"disambiguationData":[OSD([sQuery(id+"F6.wireOp",EDGE,"E47.0.1.1"),sQuery(id+"F6.wireOp",EDGE,"E47.0.1.2"),sQuery(id+"F6.wireOp",EDGE,"E47.0.1.3"),sQuery(id+"F6.wireOp",EDGE,"E47.0.1.4")])],"isStart":false})});
            var Q9;
            Q9=makeQuery(id+"F7.boolean.opBoolean","COPY",FACE,{"derivedFrom":makeQuery(id+"F7.opExtrude","CAP_FACE",FACE,{"disambiguationData":[OSD([sQuery(id+"F6.wireOp",EDGE,"E47.0.2.1"),sQuery(id+"F6.wireOp",EDGE,"E47.0.2.2"),sQuery(id+"F6.wireOp",EDGE,"E47.0.2.3"),sQuery(id+"F6.wireOp",EDGE,"E47.0.2.4")])],"isStart":false})});
            var Q10;
            Q10=makeQuery(id+"F7.boolean.opBoolean","COPY",FACE,{"derivedFrom":makeQuery(id+"F7.opExtrude","CAP_FACE",FACE,{"disambiguationData":[OSD([sQuery(id+"F6.wireOp",EDGE,"E47.0.3.1"),sQuery(id+"F6.wireOp",EDGE,"E47.0.3.2"),sQuery(id+"F6.wireOp",EDGE,"E47.0.3.3"),sQuery(id+"F6.wireOp",EDGE,"E47.0.3.4")])],"isStart":false})});
            var Q11;
            Q11=makeQuery(id+"F7.boolean.opBoolean","COPY",FACE,{"derivedFrom":makeQuery(id+"F7.opExtrude","CAP_FACE",FACE,{"disambiguationData":[OSD([sQuery(id+"F6.wireOp",EDGE,"E47.0.4.1"),sQuery(id+"F6.wireOp",EDGE,"E47.0.4.2"),sQuery(id+"F6.wireOp",EDGE,"E47.0.4.3"),sQuery(id+"F6.wireOp",EDGE,"E47.0.4.4")])],"isStart":false})});
            var Q12;
            Q12=makeQuery(id+"F7.boolean.opBoolean","COPY",FACE,{"derivedFrom":makeQuery(id+"F7.opExtrude","CAP_FACE",FACE,{"disambiguationData":[OSD([sQuery(id+"F6.wireOp",EDGE,"E47.0.5.1"),sQuery(id+"F6.wireOp",EDGE,"E47.0.5.2"),sQuery(id+"F6.wireOp",EDGE,"E47.0.5.3"),sQuery(id+"F6.wireOp",EDGE,"E47.0.5.4")])],"isStart":false})});
            var Q13;
            Q13=makeQuery(id+"F7.boolean.opBoolean","COPY",FACE,{"derivedFrom":makeQuery(id+"F7.opExtrude","CAP_FACE",FACE,{"disambiguationData":[OSD([sQuery(id+"F6.wireOp",EDGE,"E47.0.6.1"),sQuery(id+"F6.wireOp",EDGE,"E47.0.6.2"),sQuery(id+"F6.wireOp",EDGE,"E47.0.6.3"),sQuery(id+"F6.wireOp",EDGE,"E47.0.6.4")])],"isStart":false})});
            var Q14;
            Q14=makeQuery(id+"F7.boolean.opBoolean","COPY",FACE,{"derivedFrom":makeQuery(id+"F7.opExtrude","CAP_FACE",FACE,{"disambiguationData":[OSD([sQuery(id+"F6.wireOp",EDGE,"E27.9.0.5"),sQuery(id+"F6.wireOp",EDGE,"E27.9.0.6"),sQuery(id+"F6.wireOp",EDGE,"E27.9.0.7"),sQuery(id+"F6.wireOp",EDGE,"E27.9.0.8")])],"isStart":false})});
            var Q15;
            Q15=makeQuery(id+"F7.boolean.opBoolean","COPY",FACE,{"derivedFrom":makeQuery(id+"F7.opExtrude","CAP_FACE",FACE,{"disambiguationData":[OSD([sQuery(id+"F6.wireOp",EDGE,"E27.8.0.5"),sQuery(id+"F6.wireOp",EDGE,"E27.8.0.6"),sQuery(id+"F6.wireOp",EDGE,"E27.8.0.7"),sQuery(id+"F6.wireOp",EDGE,"E27.8.0.8")])],"isStart":false})});
            var Q16;
            Q16=makeQuery(id+"F7.boolean.opBoolean","COPY",FACE,{"derivedFrom":makeQuery(id+"F7.opExtrude","CAP_FACE",FACE,{"disambiguationData":[OSD([sQuery(id+"F6.wireOp",EDGE,"E27.7.0.5"),sQuery(id+"F6.wireOp",EDGE,"E27.7.0.6"),sQuery(id+"F6.wireOp",EDGE,"E27.7.0.7"),sQuery(id+"F6.wireOp",EDGE,"E27.7.0.8")])],"isStart":false})});
            var Q17;
            Q17=makeQuery(id+"F7.boolean.opBoolean","COPY",FACE,{"derivedFrom":makeQuery(id+"F7.opExtrude","CAP_FACE",FACE,{"disambiguationData":[OSD([sQuery(id+"F6.wireOp",EDGE,"E27.6.0.5"),sQuery(id+"F6.wireOp",EDGE,"E27.6.0.6"),sQuery(id+"F6.wireOp",EDGE,"E27.6.0.7"),sQuery(id+"F6.wireOp",EDGE,"E27.6.0.8")])],"isStart":false})});
            var Q18;
            Q18=makeQuery(id+"F7.boolean.opBoolean","COPY",FACE,{"derivedFrom":makeQuery(id+"F7.opExtrude","CAP_FACE",FACE,{"disambiguationData":[OSD([sQuery(id+"F6.wireOp",EDGE,"E27.5.0.5"),sQuery(id+"F6.wireOp",EDGE,"E27.5.0.6"),sQuery(id+"F6.wireOp",EDGE,"E27.5.0.7"),sQuery(id+"F6.wireOp",EDGE,"E27.5.0.8")])],"isStart":false})});
            var Q19;
            Q19=makeQuery(id+"F7.boolean.opBoolean","COPY",FACE,{"derivedFrom":makeQuery(id+"F7.opExtrude","CAP_FACE",FACE,{"disambiguationData":[OSD([sQuery(id+"F6.wireOp",EDGE,"E27.4.0.5"),sQuery(id+"F6.wireOp",EDGE,"E27.4.0.6"),sQuery(id+"F6.wireOp",EDGE,"E27.4.0.7"),sQuery(id+"F6.wireOp",EDGE,"E27.4.0.8")])],"isStart":false})});
            var Q20;
            Q20=makeQuery(id+"F7.boolean.opBoolean","COPY",FACE,{"derivedFrom":makeQuery(id+"F7.opExtrude","CAP_FACE",FACE,{"disambiguationData":[OSD([sQuery(id+"F6.wireOp",EDGE,"E40.0.1.0"),sQuery(id+"F6.wireOp",EDGE,"E40.0.1.1"),sQuery(id+"F6.wireOp",EDGE,"E40.0.1.2"),sQuery(id+"F6.wireOp",EDGE,"E40.0.1.3")])],"isStart":false})});
            var Q21;
            Q21=makeQuery(id+"F7.boolean.opBoolean","COPY",FACE,{"derivedFrom":makeQuery(id+"F7.opExtrude","CAP_FACE",FACE,{"disambiguationData":[OSD([sQuery(id+"F6.wireOp",EDGE,"E36.bottom"),sQuery(id+"F6.wireOp",EDGE,"E36.top"),sQuery(id+"F6.wireOp",EDGE,"E36.left"),sQuery(id+"F6.wireOp",EDGE,"E36.right")])],"isStart":false})});
            var Q22;
            Q22=makeQuery(id+"F7.boolean.opBoolean","COPY",FACE,{"derivedFrom":makeQuery(id+"F7.opExtrude","CAP_FACE",FACE,{"disambiguationData":[OSD([sQuery(id+"F6.wireOp",EDGE,"E39.0.1.1"),sQuery(id+"F6.wireOp",EDGE,"E39.0.1.2"),sQuery(id+"F6.wireOp",EDGE,"E39.0.1.8"),sQuery(id+"F6.wireOp",EDGE,"E39.0.1.9")])],"isStart":false})});
            var Q23;
            Q23=makeQuery(id+"F7.boolean.opBoolean","COPY",FACE,{"derivedFrom":makeQuery(id+"F7.opExtrude","CAP_FACE",FACE,{"disambiguationData":[OSD([sQuery(id+"F6.wireOp",EDGE,"E39.0.1.3"),sQuery(id+"F6.wireOp",EDGE,"E39.0.1.4"),sQuery(id+"F6.wireOp",EDGE,"E39.0.1.5"),sQuery(id+"F6.wireOp",EDGE,"E39.0.1.6")])],"isStart":false})});
            var Q24;
            Q24=makeQuery(id+"F7.boolean.opBoolean","COPY",FACE,{"derivedFrom":makeQuery(id+"F7.opExtrude","CAP_FACE",FACE,{"disambiguationData":[OSD([sQuery(id+"F6.wireOp",EDGE,"E35.bottom"),sQuery(id+"F6.wireOp",EDGE,"E35.top"),sQuery(id+"F6.wireOp",EDGE,"E35.left"),sQuery(id+"F6.wireOp",EDGE,"E35.right")])],"isStart":false})});
            var Q25;
            Q25=makeQuery(id+"F7.boolean.opBoolean","COPY",FACE,{"derivedFrom":makeQuery(id+"F7.opExtrude","CAP_FACE",FACE,{"disambiguationData":[OSD([sQuery(id+"F6.wireOp",EDGE,"E40.0.1.4"),sQuery(id+"F6.wireOp",EDGE,"E40.0.1.5"),sQuery(id+"F6.wireOp",EDGE,"E40.0.1.6"),sQuery(id+"F6.wireOp",EDGE,"E40.0.1.7")])],"isStart":false})});
            var Q26;
            Q26=makeQuery(id+"F7.boolean.opBoolean","COPY",FACE,{"derivedFrom":makeQuery(id+"F7.opExtrude","CAP_FACE",FACE,{"disambiguationData":[OSD([sQuery(id+"F6.wireOp",EDGE,"E34.3.0.1"),sQuery(id+"F6.wireOp",EDGE,"E34.3.0.2"),sQuery(id+"F6.wireOp",EDGE,"E34.3.0.3"),sQuery(id+"F6.wireOp",EDGE,"E34.3.0.5")])],"isStart":false})});
            var Q27;
            Q27=makeQuery(id+"F7.boolean.opBoolean","COPY",FACE,{"derivedFrom":makeQuery(id+"F7.opExtrude","CAP_FACE",FACE,{"disambiguationData":[OSD([sQuery(id+"F6.wireOp",EDGE,"E34.2.0.1"),sQuery(id+"F6.wireOp",EDGE,"E34.2.0.2"),sQuery(id+"F6.wireOp",EDGE,"E34.2.0.3"),sQuery(id+"F6.wireOp",EDGE,"E34.2.0.5")])],"isStart":false})});
            var Q28;
            Q28=makeQuery(id+"F7.boolean.opBoolean","COPY",FACE,{"derivedFrom":makeQuery(id+"F7.opExtrude","CAP_FACE",FACE,{"disambiguationData":[OSD([sQuery(id+"F6.wireOp",EDGE,"E34.1.0.1"),sQuery(id+"F6.wireOp",EDGE,"E34.1.0.2"),sQuery(id+"F6.wireOp",EDGE,"E34.1.0.3"),sQuery(id+"F6.wireOp",EDGE,"E34.1.0.5")])],"isStart":false})});
            var Q29;
            Q29=makeQuery(id+"F7.boolean.opBoolean","COPY",FACE,{"derivedFrom":makeQuery(id+"F7.opExtrude","CAP_FACE",FACE,{"disambiguationData":[OSD([sQuery(id+"F6.wireOp",EDGE,"E30.bottom"),sQuery(id+"F6.wireOp",EDGE,"E30.top"),sQuery(id+"F6.wireOp",EDGE,"E30.left"),sQuery(id+"F6.wireOp",EDGE,"E30.right")])],"isStart":false})});
            var Q30;
            Q30=makeQuery(id+"F7.boolean.opBoolean","COPY",FACE,{"derivedFrom":makeQuery(id+"F7.opExtrude","CAP_FACE",FACE,{"disambiguationData":[OSD([sQuery(id+"F6.wireOp",EDGE,"E33.1.0.11"),sQuery(id+"F6.wireOp",EDGE,"E33.1.0.12"),sQuery(id+"F6.wireOp",EDGE,"E33.1.0.15"),sQuery(id+"F6.wireOp",EDGE,"E33.1.0.17")])],"isStart":false})});
            var Q31;
            Q31=makeQuery(id+"F7.boolean.opBoolean","COPY",FACE,{"derivedFrom":makeQuery(id+"F7.opExtrude","CAP_FACE",FACE,{"disambiguationData":[OSD([sQuery(id+"F6.wireOp",EDGE,"E33.2.0.11"),sQuery(id+"F6.wireOp",EDGE,"E33.2.0.12"),sQuery(id+"F6.wireOp",EDGE,"E33.2.0.15"),sQuery(id+"F6.wireOp",EDGE,"E33.2.0.17")])],"isStart":false})});
            var Q32;
            Q32=makeQuery(id+"F7.boolean.opBoolean","COPY",FACE,{"derivedFrom":makeQuery(id+"F7.opExtrude","CAP_FACE",FACE,{"disambiguationData":[OSD([sQuery(id+"F6.wireOp",EDGE,"E33.3.0.11"),sQuery(id+"F6.wireOp",EDGE,"E33.3.0.12"),sQuery(id+"F6.wireOp",EDGE,"E33.3.0.15"),sQuery(id+"F6.wireOp",EDGE,"E33.3.0.17")])],"isStart":false})});
            var Q33;
            Q33=makeQuery(id+"F7.boolean.opBoolean","COPY",FACE,{"derivedFrom":makeQuery(id+"F7.opExtrude","CAP_FACE",FACE,{"disambiguationData":[OSD([sQuery(id+"F6.wireOp",EDGE,"E33.3.0.10"),sQuery(id+"F6.wireOp",EDGE,"E33.3.0.18"),sQuery(id+"F6.wireOp",EDGE,"E33.3.0.19"),sQuery(id+"F6.wireOp",EDGE,"E33.3.0.20")])],"isStart":false})});
            var Q34;
            Q34=makeQuery(id+"F7.boolean.opBoolean","COPY",FACE,{"derivedFrom":makeQuery(id+"F7.opExtrude","CAP_FACE",FACE,{"disambiguationData":[OSD([sQuery(id+"F6.wireOp",EDGE,"E33.2.0.10"),sQuery(id+"F6.wireOp",EDGE,"E33.2.0.18"),sQuery(id+"F6.wireOp",EDGE,"E33.2.0.19"),sQuery(id+"F6.wireOp",EDGE,"E33.2.0.20")])],"isStart":false})});
            var Q35;
            Q35=makeQuery(id+"F7.boolean.opBoolean","COPY",FACE,{"derivedFrom":makeQuery(id+"F7.opExtrude","CAP_FACE",FACE,{"disambiguationData":[OSD([sQuery(id+"F6.wireOp",EDGE,"E33.1.0.10"),sQuery(id+"F6.wireOp",EDGE,"E33.1.0.18"),sQuery(id+"F6.wireOp",EDGE,"E33.1.0.19"),sQuery(id+"F6.wireOp",EDGE,"E33.1.0.20")])],"isStart":false})});
            var Q36;
            Q36=makeQuery(id+"F7.boolean.opBoolean","COPY",FACE,{"derivedFrom":makeQuery(id+"F7.opExtrude","CAP_FACE",FACE,{"disambiguationData":[OSD([sQuery(id+"F6.wireOp",EDGE,"E29.bottom"),sQuery(id+"F6.wireOp",EDGE,"E29.top"),sQuery(id+"F6.wireOp",EDGE,"E29.left"),sQuery(id+"F6.wireOp",EDGE,"E29.right")])],"isStart":false})});
            var Q37;
            Q37=makeQuery(id+"F7.boolean.opBoolean","COPY",FACE,{"derivedFrom":makeQuery(id+"F7.opExtrude","CAP_FACE",FACE,{"disambiguationData":[OSD([sQuery(id+"F6.wireOp",EDGE,"E34.1.0.6"),sQuery(id+"F6.wireOp",EDGE,"E34.1.0.8"),sQuery(id+"F6.wireOp",EDGE,"E34.1.0.9"),sQuery(id+"F6.wireOp",EDGE,"E34.1.0.10")])],"isStart":false})});
            var Q38;
            Q38=makeQuery(id+"F7.boolean.opBoolean","COPY",FACE,{"derivedFrom":makeQuery(id+"F7.opExtrude","CAP_FACE",FACE,{"disambiguationData":[OSD([sQuery(id+"F6.wireOp",EDGE,"E34.2.0.6"),sQuery(id+"F6.wireOp",EDGE,"E34.2.0.8"),sQuery(id+"F6.wireOp",EDGE,"E34.2.0.9"),sQuery(id+"F6.wireOp",EDGE,"E34.2.0.10")])],"isStart":false})});
            var Q39;
            Q39=makeQuery(id+"F7.boolean.opBoolean","COPY",FACE,{"derivedFrom":makeQuery(id+"F7.opExtrude","CAP_FACE",FACE,{"disambiguationData":[OSD([sQuery(id+"F6.wireOp",EDGE,"E34.3.0.6"),sQuery(id+"F6.wireOp",EDGE,"E34.3.0.8"),sQuery(id+"F6.wireOp",EDGE,"E34.3.0.9"),sQuery(id+"F6.wireOp",EDGE,"E34.3.0.10")])],"isStart":false})});
            var Q40;
            Q40=makeQuery(id+"F7.boolean.opBoolean","COPY",FACE,{"derivedFrom":makeQuery(id+"F7.opExtrude","CAP_FACE",FACE,{"disambiguationData":[OSD([sQuery(id+"F6.wireOp",EDGE,"E27.3.0.5"),sQuery(id+"F6.wireOp",EDGE,"E27.3.0.6"),sQuery(id+"F6.wireOp",EDGE,"E27.3.0.7"),sQuery(id+"F6.wireOp",EDGE,"E27.3.0.8")])],"isStart":false})});
            var Q41;
            Q41=makeQuery(id+"F7.boolean.opBoolean","COPY",FACE,{"derivedFrom":makeQuery(id+"F7.opExtrude","CAP_FACE",FACE,{"disambiguationData":[OSD([sQuery(id+"F6.wireOp",EDGE,"E27.2.0.5"),sQuery(id+"F6.wireOp",EDGE,"E27.2.0.6"),sQuery(id+"F6.wireOp",EDGE,"E27.2.0.7"),sQuery(id+"F6.wireOp",EDGE,"E27.2.0.8")])],"isStart":false})});
            var Q42;
            Q42=makeQuery(id+"F7.boolean.opBoolean","COPY",FACE,{"derivedFrom":makeQuery(id+"F7.opExtrude","CAP_FACE",FACE,{"disambiguationData":[OSD([sQuery(id+"F6.wireOp",EDGE,"E27.1.0.5"),sQuery(id+"F6.wireOp",EDGE,"E27.1.0.6"),sQuery(id+"F6.wireOp",EDGE,"E27.1.0.7"),sQuery(id+"F6.wireOp",EDGE,"E27.1.0.8")])],"isStart":false})});
            var Q43;
            Q43=makeQuery(id+"F7.boolean.opBoolean","COPY",FACE,{"derivedFrom":makeQuery(id+"F7.opExtrude","CAP_FACE",FACE,{"disambiguationData":[OSD([sQuery(id+"F6.wireOp",EDGE,"E26.bottom"),sQuery(id+"F6.wireOp",EDGE,"E26.top"),sQuery(id+"F6.wireOp",EDGE,"E26.left"),sQuery(id+"F6.wireOp",EDGE,"E26.right")])],"isStart":false})});
            var Q44;
            Q44=makeQuery(id+"F7.boolean.opBoolean","COPY",FACE,{"derivedFrom":makeQuery(id+"F7.opExtrude","CAP_FACE",FACE,{"disambiguationData":[OSD([sQuery(id+"F6.wireOp",EDGE,"E28.1.0.5"),sQuery(id+"F6.wireOp",EDGE,"E28.1.0.6"),sQuery(id+"F6.wireOp",EDGE,"E28.1.0.8"),sQuery(id+"F6.wireOp",EDGE,"E28.1.0.9")])],"isStart":false})});
            var Q45;
            Q45=makeQuery(id+"F7.boolean.opBoolean","COPY",FACE,{"derivedFrom":makeQuery(id+"F7.opExtrude","CAP_FACE",FACE,{"disambiguationData":[OSD([sQuery(id+"F6.wireOp",EDGE,"E28.2.0.5"),sQuery(id+"F6.wireOp",EDGE,"E28.2.0.6"),sQuery(id+"F6.wireOp",EDGE,"E28.2.0.8"),sQuery(id+"F6.wireOp",EDGE,"E28.2.0.9")])],"isStart":false})});
            var Q46;
            Q46=makeQuery(id+"F7.boolean.opBoolean","COPY",FACE,{"derivedFrom":makeQuery(id+"F7.opExtrude","CAP_FACE",FACE,{"disambiguationData":[OSD([sQuery(id+"F6.wireOp",EDGE,"E28.3.0.5"),sQuery(id+"F6.wireOp",EDGE,"E28.3.0.6"),sQuery(id+"F6.wireOp",EDGE,"E28.3.0.8"),sQuery(id+"F6.wireOp",EDGE,"E28.3.0.9")])],"isStart":false})});
            var Q47;
            Q47=makeQuery(id+"F7.boolean.opBoolean","COPY",FACE,{"derivedFrom":makeQuery(id+"F7.opExtrude","CAP_FACE",FACE,{"disambiguationData":[OSD([sQuery(id+"F6.wireOp",EDGE,"E28.4.0.5"),sQuery(id+"F6.wireOp",EDGE,"E28.4.0.6"),sQuery(id+"F6.wireOp",EDGE,"E28.4.0.8"),sQuery(id+"F6.wireOp",EDGE,"E28.4.0.9")])],"isStart":false})});
            var Q48;
            Q48=makeQuery(id+"F7.boolean.opBoolean","COPY",FACE,{"derivedFrom":makeQuery(id+"F7.opExtrude","CAP_FACE",FACE,{"disambiguationData":[OSD([sQuery(id+"F6.wireOp",EDGE,"E28.5.0.5"),sQuery(id+"F6.wireOp",EDGE,"E28.5.0.6"),sQuery(id+"F6.wireOp",EDGE,"E28.5.0.8"),sQuery(id+"F6.wireOp",EDGE,"E28.5.0.9")])],"isStart":false})});
            var Q49;
            Q49=makeQuery(id+"F7.boolean.opBoolean","COPY",FACE,{"derivedFrom":makeQuery(id+"F7.opExtrude","CAP_FACE",FACE,{"disambiguationData":[OSD([sQuery(id+"F6.wireOp",EDGE,"E28.6.0.5"),sQuery(id+"F6.wireOp",EDGE,"E28.6.0.6"),sQuery(id+"F6.wireOp",EDGE,"E28.6.0.8"),sQuery(id+"F6.wireOp",EDGE,"E28.6.0.9")])],"isStart":false})});
            var Q50;
            Q50=makeQuery(id+"F7.boolean.opBoolean","COPY",FACE,{"derivedFrom":makeQuery(id+"F7.opExtrude","CAP_FACE",FACE,{"disambiguationData":[OSD([sQuery(id+"F6.wireOp",EDGE,"E28.7.0.5"),sQuery(id+"F6.wireOp",EDGE,"E28.7.0.6"),sQuery(id+"F6.wireOp",EDGE,"E28.7.0.8"),sQuery(id+"F6.wireOp",EDGE,"E28.7.0.9")])],"isStart":false})});
            var Q51;
            Q51=makeQuery(id+"F7.boolean.opBoolean","COPY",FACE,{"derivedFrom":makeQuery(id+"F7.opExtrude","CAP_FACE",FACE,{"disambiguationData":[OSD([sQuery(id+"F6.wireOp",EDGE,"E28.8.0.5"),sQuery(id+"F6.wireOp",EDGE,"E28.8.0.6"),sQuery(id+"F6.wireOp",EDGE,"E28.8.0.8"),sQuery(id+"F6.wireOp",EDGE,"E28.8.0.9")])],"isStart":false})});
            var Q52;
            Q52=makeQuery(id+"F7.boolean.opBoolean","COPY",FACE,{"derivedFrom":makeQuery(id+"F7.opExtrude","CAP_FACE",FACE,{"disambiguationData":[OSD([sQuery(id+"F6.wireOp",EDGE,"E28.9.0.5"),sQuery(id+"F6.wireOp",EDGE,"E28.9.0.6"),sQuery(id+"F6.wireOp",EDGE,"E28.9.0.8"),sQuery(id+"F6.wireOp",EDGE,"E28.9.0.9")])],"isStart":false})});
            var Q53;
            Q53=makeQuery(id+"F7.boolean.opBoolean","COPY",FACE,{"derivedFrom":makeQuery(id+"F7.opExtrude","CAP_FACE",FACE,{"disambiguationData":[OSD([sQuery(id+"F6.wireOp",EDGE,"E42.0.13.0"),sQuery(id+"F6.wireOp",EDGE,"E42.0.13.1"),sQuery(id+"F6.wireOp",EDGE,"E42.0.13.2"),sQuery(id+"F6.wireOp",EDGE,"E42.0.13.3")])],"isStart":false})});
            var Q54;
            Q54=makeQuery(id+"F7.boolean.opBoolean","COPY",FACE,{"derivedFrom":makeQuery(id+"F7.opExtrude","CAP_FACE",FACE,{"disambiguationData":[OSD([sQuery(id+"F6.wireOp",EDGE,"E42.0.12.0"),sQuery(id+"F6.wireOp",EDGE,"E42.0.12.1"),sQuery(id+"F6.wireOp",EDGE,"E42.0.12.2"),sQuery(id+"F6.wireOp",EDGE,"E42.0.12.3")])],"isStart":false})});
            var Q55;
            Q55=makeQuery(id+"F7.boolean.opBoolean","COPY",FACE,{"derivedFrom":makeQuery(id+"F7.opExtrude","CAP_FACE",FACE,{"disambiguationData":[OSD([sQuery(id+"F6.wireOp",EDGE,"E42.0.11.0"),sQuery(id+"F6.wireOp",EDGE,"E42.0.11.1"),sQuery(id+"F6.wireOp",EDGE,"E42.0.11.2"),sQuery(id+"F6.wireOp",EDGE,"E42.0.11.3")])],"isStart":false})});
            var Q56;
            Q56=makeQuery(id+"F7.boolean.opBoolean","COPY",FACE,{"derivedFrom":makeQuery(id+"F7.opExtrude","CAP_FACE",FACE,{"disambiguationData":[OSD([sQuery(id+"F6.wireOp",EDGE,"E42.0.10.0"),sQuery(id+"F6.wireOp",EDGE,"E42.0.10.1"),sQuery(id+"F6.wireOp",EDGE,"E42.0.10.2"),sQuery(id+"F6.wireOp",EDGE,"E42.0.10.3")])],"isStart":false})});
            var Q57;
            Q57=makeQuery(id+"F7.boolean.opBoolean","COPY",FACE,{"derivedFrom":makeQuery(id+"F7.opExtrude","CAP_FACE",FACE,{"disambiguationData":[OSD([sQuery(id+"F6.wireOp",EDGE,"E42.0.9.0"),sQuery(id+"F6.wireOp",EDGE,"E42.0.9.1"),sQuery(id+"F6.wireOp",EDGE,"E42.0.9.2"),sQuery(id+"F6.wireOp",EDGE,"E42.0.9.3")])],"isStart":false})});
            var Q58;
            Q58=makeQuery(id+"F7.boolean.opBoolean","COPY",FACE,{"derivedFrom":makeQuery(id+"F7.opExtrude","CAP_FACE",FACE,{"disambiguationData":[OSD([sQuery(id+"F6.wireOp",EDGE,"E40.0.1.12"),sQuery(id+"F6.wireOp",EDGE,"E40.0.1.14"),sQuery(id+"F6.wireOp",EDGE,"E40.0.1.15"),sQuery(id+"F6.wireOp",EDGE,"E40.0.1.16")])],"isStart":false})});
            var Q59;
            Q59=makeQuery(id+"F7.boolean.opBoolean","COPY",FACE,{"derivedFrom":makeQuery(id+"F7.opExtrude","CAP_FACE",FACE,{"disambiguationData":[OSD([sQuery(id+"F6.wireOp",EDGE,"E40.0.1.10"),sQuery(id+"F6.wireOp",EDGE,"E40.0.1.11"),sQuery(id+"F6.wireOp",EDGE,"E40.0.1.13"),sQuery(id+"F6.wireOp",EDGE,"E40.0.1.19")])],"isStart":false})});
            var Q60;
            Q60=makeQuery(id+"F7.boolean.opBoolean","COPY",FACE,{"derivedFrom":makeQuery(id+"F7.opExtrude","CAP_FACE",FACE,{"disambiguationData":[OSD([sQuery(id+"F6.wireOp",EDGE,"E37.bottom"),sQuery(id+"F6.wireOp",EDGE,"E37.top"),sQuery(id+"F6.wireOp",EDGE,"E37.left"),sQuery(id+"F6.wireOp",EDGE,"E37.right")])],"isStart":false})});
            var Q61;
            Q61=makeQuery(id+"F7.boolean.opBoolean","COPY",FACE,{"derivedFrom":makeQuery(id+"F7.opExtrude","CAP_FACE",FACE,{"disambiguationData":[OSD([sQuery(id+"F6.wireOp",EDGE,"E39.0.1.10"),sQuery(id+"F6.wireOp",EDGE,"E39.0.1.11"),sQuery(id+"F6.wireOp",EDGE,"E39.0.1.13"),sQuery(id+"F6.wireOp",EDGE,"E39.0.1.19")])],"isStart":false})});
            var Q62;
            Q62=makeQuery(id+"F7.boolean.opBoolean","COPY",FACE,{"derivedFrom":makeQuery(id+"F7.opExtrude","CAP_FACE",FACE,{"disambiguationData":[OSD([sQuery(id+"F6.wireOp",EDGE,"E39.0.1.14"),sQuery(id+"F6.wireOp",EDGE,"E39.0.1.16"),sQuery(id+"F6.wireOp",EDGE,"E39.0.1.17"),sQuery(id+"F6.wireOp",EDGE,"E39.0.1.18")])],"isStart":false})});
            var Q63;
            Q63=makeQuery(id+"F7.boolean.opBoolean","COPY",FACE,{"derivedFrom":makeQuery(id+"F7.opExtrude","CAP_FACE",FACE,{"disambiguationData":[OSD([sQuery(id+"F6.wireOp",EDGE,"E38.bottom"),sQuery(id+"F6.wireOp",EDGE,"E38.top"),sQuery(id+"F6.wireOp",EDGE,"E38.left"),sQuery(id+"F6.wireOp",EDGE,"E38.right")])],"isStart":false})});
            var Q64;
            Q64=makeQuery(id+"F7.boolean.opBoolean","COPY",FACE,{"derivedFrom":makeQuery(id+"F7.opExtrude","CAP_FACE",FACE,{"disambiguationData":[OSD([sQuery(id+"F6.wireOp",EDGE,"E42.0.8.0"),sQuery(id+"F6.wireOp",EDGE,"E42.0.8.1"),sQuery(id+"F6.wireOp",EDGE,"E42.0.8.2"),sQuery(id+"F6.wireOp",EDGE,"E42.0.8.3")])],"isStart":false})});
            var Q65;
            Q65=makeQuery(id+"F7.boolean.opBoolean","COPY",FACE,{"derivedFrom":makeQuery(id+"F7.opExtrude","CAP_FACE",FACE,{"disambiguationData":[OSD([sQuery(id+"F6.wireOp",EDGE,"E42.0.7.0"),sQuery(id+"F6.wireOp",EDGE,"E42.0.7.1"),sQuery(id+"F6.wireOp",EDGE,"E42.0.7.2"),sQuery(id+"F6.wireOp",EDGE,"E42.0.7.3")])],"isStart":false})});
            var Q66;
            Q66=makeQuery(id+"F7.boolean.opBoolean","COPY",FACE,{"derivedFrom":makeQuery(id+"F7.opExtrude","CAP_FACE",FACE,{"disambiguationData":[OSD([sQuery(id+"F6.wireOp",EDGE,"E42.0.6.0"),sQuery(id+"F6.wireOp",EDGE,"E42.0.6.1"),sQuery(id+"F6.wireOp",EDGE,"E42.0.6.2"),sQuery(id+"F6.wireOp",EDGE,"E42.0.6.3")])],"isStart":false})});
            var Q67;
            Q67=makeQuery(id+"F7.boolean.opBoolean","COPY",FACE,{"derivedFrom":makeQuery(id+"F7.opExtrude","CAP_FACE",FACE,{"disambiguationData":[OSD([sQuery(id+"F6.wireOp",EDGE,"E42.0.5.0"),sQuery(id+"F6.wireOp",EDGE,"E42.0.5.1"),sQuery(id+"F6.wireOp",EDGE,"E42.0.5.2"),sQuery(id+"F6.wireOp",EDGE,"E42.0.5.3")])],"isStart":false})});
            var Q68;
            Q68=makeQuery(id+"F7.boolean.opBoolean","COPY",FACE,{"derivedFrom":makeQuery(id+"F7.opExtrude","CAP_FACE",FACE,{"disambiguationData":[OSD([sQuery(id+"F6.wireOp",EDGE,"E42.0.4.0"),sQuery(id+"F6.wireOp",EDGE,"E42.0.4.1"),sQuery(id+"F6.wireOp",EDGE,"E42.0.4.2"),sQuery(id+"F6.wireOp",EDGE,"E42.0.4.3")])],"isStart":false})});
            var Q69;
            Q69=makeQuery(id+"F7.boolean.opBoolean","COPY",FACE,{"derivedFrom":makeQuery(id+"F7.opExtrude","CAP_FACE",FACE,{"disambiguationData":[OSD([sQuery(id+"F6.wireOp",EDGE,"E34.3.0.16"),sQuery(id+"F6.wireOp",EDGE,"E34.3.0.18"),sQuery(id+"F6.wireOp",EDGE,"E34.3.0.19"),sQuery(id+"F6.wireOp",EDGE,"E34.3.0.20")])],"isStart":false})});
            var Q70;
            Q70=makeQuery(id+"F7.boolean.opBoolean","COPY",FACE,{"derivedFrom":makeQuery(id+"F7.opExtrude","CAP_FACE",FACE,{"disambiguationData":[OSD([sQuery(id+"F6.wireOp",EDGE,"E34.3.0.12"),sQuery(id+"F6.wireOp",EDGE,"E34.3.0.13"),sQuery(id+"F6.wireOp",EDGE,"E34.3.0.14"),sQuery(id+"F6.wireOp",EDGE,"E34.3.0.15")])],"isStart":false})});
            var Q71;
            Q71=makeQuery(id+"F7.boolean.opBoolean","COPY",FACE,{"derivedFrom":makeQuery(id+"F7.opExtrude","CAP_FACE",FACE,{"disambiguationData":[OSD([sQuery(id+"F6.wireOp",EDGE,"E34.2.0.12"),sQuery(id+"F6.wireOp",EDGE,"E34.2.0.13"),sQuery(id+"F6.wireOp",EDGE,"E34.2.0.14"),sQuery(id+"F6.wireOp",EDGE,"E34.2.0.15")])],"isStart":false})});
            var Q72;
            Q72=makeQuery(id+"F7.boolean.opBoolean","COPY",FACE,{"derivedFrom":makeQuery(id+"F7.opExtrude","CAP_FACE",FACE,{"disambiguationData":[OSD([sQuery(id+"F6.wireOp",EDGE,"E34.2.0.16"),sQuery(id+"F6.wireOp",EDGE,"E34.2.0.18"),sQuery(id+"F6.wireOp",EDGE,"E34.2.0.19"),sQuery(id+"F6.wireOp",EDGE,"E34.2.0.20")])],"isStart":false})});
            var Q73;
            Q73=makeQuery(id+"F7.boolean.opBoolean","COPY",FACE,{"derivedFrom":makeQuery(id+"F7.opExtrude","CAP_FACE",FACE,{"disambiguationData":[OSD([sQuery(id+"F6.wireOp",EDGE,"E34.1.0.12"),sQuery(id+"F6.wireOp",EDGE,"E34.1.0.13"),sQuery(id+"F6.wireOp",EDGE,"E34.1.0.14"),sQuery(id+"F6.wireOp",EDGE,"E34.1.0.15")])],"isStart":false})});
            var Q74;
            Q74=makeQuery(id+"F7.boolean.opBoolean","COPY",FACE,{"derivedFrom":makeQuery(id+"F7.opExtrude","CAP_FACE",FACE,{"disambiguationData":[OSD([sQuery(id+"F6.wireOp",EDGE,"E32.bottom"),sQuery(id+"F6.wireOp",EDGE,"E32.top"),sQuery(id+"F6.wireOp",EDGE,"E32.left"),sQuery(id+"F6.wireOp",EDGE,"E32.right")])],"isStart":false})});
            var Q75;
            Q75=makeQuery(id+"F7.boolean.opBoolean","COPY",FACE,{"derivedFrom":makeQuery(id+"F7.opExtrude","CAP_FACE",FACE,{"disambiguationData":[OSD([sQuery(id+"F6.wireOp",EDGE,"E31.bottom"),sQuery(id+"F6.wireOp",EDGE,"E31.top"),sQuery(id+"F6.wireOp",EDGE,"E31.left"),sQuery(id+"F6.wireOp",EDGE,"E31.right")])],"isStart":false})});
            var Q76;
            Q76=makeQuery(id+"F7.boolean.opBoolean","COPY",FACE,{"derivedFrom":makeQuery(id+"F7.opExtrude","CAP_FACE",FACE,{"disambiguationData":[OSD([sQuery(id+"F6.wireOp",EDGE,"E33.1.0.4"),sQuery(id+"F6.wireOp",EDGE,"E33.1.0.5"),sQuery(id+"F6.wireOp",EDGE,"E33.1.0.7"),sQuery(id+"F6.wireOp",EDGE,"E33.1.0.8")])],"isStart":false})});
            var Q77;
            Q77=makeQuery(id+"F7.boolean.opBoolean","COPY",FACE,{"derivedFrom":makeQuery(id+"F7.opExtrude","CAP_FACE",FACE,{"disambiguationData":[OSD([sQuery(id+"F6.wireOp",EDGE,"E33.1.0.0"),sQuery(id+"F6.wireOp",EDGE,"E33.1.0.1"),sQuery(id+"F6.wireOp",EDGE,"E33.1.0.2"),sQuery(id+"F6.wireOp",EDGE,"E33.1.0.6")])],"isStart":false})});
            var Q78;
            Q78=makeQuery(id+"F7.boolean.opBoolean","COPY",FACE,{"derivedFrom":makeQuery(id+"F7.opExtrude","CAP_FACE",FACE,{"disambiguationData":[OSD([sQuery(id+"F6.wireOp",EDGE,"E33.2.0.0"),sQuery(id+"F6.wireOp",EDGE,"E33.2.0.1"),sQuery(id+"F6.wireOp",EDGE,"E33.2.0.2"),sQuery(id+"F6.wireOp",EDGE,"E33.2.0.6")])],"isStart":false})});
            var Q79;
            Q79=makeQuery(id+"F7.boolean.opBoolean","COPY",FACE,{"derivedFrom":makeQuery(id+"F7.opExtrude","CAP_FACE",FACE,{"disambiguationData":[OSD([sQuery(id+"F6.wireOp",EDGE,"E33.2.0.4"),sQuery(id+"F6.wireOp",EDGE,"E33.2.0.5"),sQuery(id+"F6.wireOp",EDGE,"E33.2.0.7"),sQuery(id+"F6.wireOp",EDGE,"E33.2.0.8")])],"isStart":false})});
            var Q80;
            Q80=makeQuery(id+"F7.boolean.opBoolean","COPY",FACE,{"derivedFrom":makeQuery(id+"F7.opExtrude","CAP_FACE",FACE,{"disambiguationData":[OSD([sQuery(id+"F6.wireOp",EDGE,"E33.3.0.4"),sQuery(id+"F6.wireOp",EDGE,"E33.3.0.5"),sQuery(id+"F6.wireOp",EDGE,"E33.3.0.7"),sQuery(id+"F6.wireOp",EDGE,"E33.3.0.8")])],"isStart":false})});
            var Q81;
            Q81=makeQuery(id+"F7.boolean.opBoolean","COPY",FACE,{"derivedFrom":makeQuery(id+"F7.opExtrude","CAP_FACE",FACE,{"disambiguationData":[OSD([sQuery(id+"F6.wireOp",EDGE,"E33.3.0.0"),sQuery(id+"F6.wireOp",EDGE,"E33.3.0.1"),sQuery(id+"F6.wireOp",EDGE,"E33.3.0.2"),sQuery(id+"F6.wireOp",EDGE,"E33.3.0.6")])],"isStart":false})});
            var Q82;
            Q82=makeQuery(id+"F7.boolean.opBoolean","COPY",FACE,{"derivedFrom":makeQuery(id+"F7.opExtrude","CAP_FACE",FACE,{"disambiguationData":[OSD([sQuery(id+"F6.wireOp",EDGE,"E42.0.3.0"),sQuery(id+"F6.wireOp",EDGE,"E42.0.3.1"),sQuery(id+"F6.wireOp",EDGE,"E42.0.3.2"),sQuery(id+"F6.wireOp",EDGE,"E42.0.3.3")])],"isStart":false})});
            var Q83;
            Q83=makeQuery(id+"F7.boolean.opBoolean","COPY",FACE,{"derivedFrom":makeQuery(id+"F7.opExtrude","CAP_FACE",FACE,{"disambiguationData":[OSD([sQuery(id+"F6.wireOp",EDGE,"E42.0.2.0"),sQuery(id+"F6.wireOp",EDGE,"E42.0.2.1"),sQuery(id+"F6.wireOp",EDGE,"E42.0.2.2"),sQuery(id+"F6.wireOp",EDGE,"E42.0.2.3")])],"isStart":false})});
            var Q84;
            Q84=makeQuery(id+"F7.boolean.opBoolean","COPY",FACE,{"derivedFrom":makeQuery(id+"F7.opExtrude","CAP_FACE",FACE,{"disambiguationData":[OSD([sQuery(id+"F6.wireOp",EDGE,"E42.0.1.0"),sQuery(id+"F6.wireOp",EDGE,"E42.0.1.1"),sQuery(id+"F6.wireOp",EDGE,"E42.0.1.2"),sQuery(id+"F6.wireOp",EDGE,"E42.0.1.3")])],"isStart":false})});
            var Q85;
            Q85=makeQuery(id+"F7.boolean.opBoolean","COPY",FACE,{"derivedFrom":makeQuery(id+"F7.opExtrude","CAP_FACE",FACE,{"disambiguationData":[OSD([sQuery(id+"F6.wireOp",EDGE,"E41.bottom"),sQuery(id+"F6.wireOp",EDGE,"E41.top"),sQuery(id+"F6.wireOp",EDGE,"E41.left"),sQuery(id+"F6.wireOp",EDGE,"E41.right")])],"isStart":false})});
            var Q86;
            Q86=makeQuery(id+"F7.boolean.opBoolean","COPY",FACE,{"derivedFrom":makeQuery(id+"F7.opExtrude","CAP_FACE",FACE,{"disambiguationData":[OSD([sQuery(id+"F6.wireOp",EDGE,"E28.9.0.0"),sQuery(id+"F6.wireOp",EDGE,"E28.9.0.1"),sQuery(id+"F6.wireOp",EDGE,"E28.9.0.2"),sQuery(id+"F6.wireOp",EDGE,"E28.9.0.3")])],"isStart":false})});
            var Q87;
            Q87=makeQuery(id+"F7.boolean.opBoolean","COPY",FACE,{"derivedFrom":makeQuery(id+"F7.opExtrude","CAP_FACE",FACE,{"disambiguationData":[OSD([sQuery(id+"F6.wireOp",EDGE,"E28.8.0.0"),sQuery(id+"F6.wireOp",EDGE,"E28.8.0.1"),sQuery(id+"F6.wireOp",EDGE,"E28.8.0.2"),sQuery(id+"F6.wireOp",EDGE,"E28.8.0.3")])],"isStart":false})});
            var Q88;
            Q88=makeQuery(id+"F7.boolean.opBoolean","COPY",FACE,{"derivedFrom":makeQuery(id+"F7.opExtrude","CAP_FACE",FACE,{"disambiguationData":[OSD([sQuery(id+"F6.wireOp",EDGE,"E28.7.0.0"),sQuery(id+"F6.wireOp",EDGE,"E28.7.0.1"),sQuery(id+"F6.wireOp",EDGE,"E28.7.0.2"),sQuery(id+"F6.wireOp",EDGE,"E28.7.0.3")])],"isStart":false})});
            var Q89;
            Q89=makeQuery(id+"F7.boolean.opBoolean","COPY",FACE,{"derivedFrom":makeQuery(id+"F7.opExtrude","CAP_FACE",FACE,{"disambiguationData":[OSD([sQuery(id+"F6.wireOp",EDGE,"E28.6.0.0"),sQuery(id+"F6.wireOp",EDGE,"E28.6.0.1"),sQuery(id+"F6.wireOp",EDGE,"E28.6.0.2"),sQuery(id+"F6.wireOp",EDGE,"E28.6.0.3")])],"isStart":false})});
            var Q90;
            Q90=makeQuery(id+"F7.boolean.opBoolean","COPY",FACE,{"derivedFrom":makeQuery(id+"F7.opExtrude","CAP_FACE",FACE,{"disambiguationData":[OSD([sQuery(id+"F6.wireOp",EDGE,"E28.5.0.0"),sQuery(id+"F6.wireOp",EDGE,"E28.5.0.1"),sQuery(id+"F6.wireOp",EDGE,"E28.5.0.2"),sQuery(id+"F6.wireOp",EDGE,"E28.5.0.3")])],"isStart":false})});
            var Q91;
            Q91=makeQuery(id+"F7.boolean.opBoolean","COPY",FACE,{"derivedFrom":makeQuery(id+"F7.opExtrude","CAP_FACE",FACE,{"disambiguationData":[OSD([sQuery(id+"F6.wireOp",EDGE,"E28.4.0.0"),sQuery(id+"F6.wireOp",EDGE,"E28.4.0.1"),sQuery(id+"F6.wireOp",EDGE,"E28.4.0.2"),sQuery(id+"F6.wireOp",EDGE,"E28.4.0.3")])],"isStart":false})});
            var Q92;
            Q92=makeQuery(id+"F7.boolean.opBoolean","COPY",FACE,{"derivedFrom":makeQuery(id+"F7.opExtrude","CAP_FACE",FACE,{"disambiguationData":[OSD([sQuery(id+"F6.wireOp",EDGE,"E28.3.0.0"),sQuery(id+"F6.wireOp",EDGE,"E28.3.0.1"),sQuery(id+"F6.wireOp",EDGE,"E28.3.0.2"),sQuery(id+"F6.wireOp",EDGE,"E28.3.0.3")])],"isStart":false})});
            var Q93;
            Q93=makeQuery(id+"F7.boolean.opBoolean","COPY",FACE,{"derivedFrom":makeQuery(id+"F7.opExtrude","CAP_FACE",FACE,{"disambiguationData":[OSD([sQuery(id+"F6.wireOp",EDGE,"E28.2.0.0"),sQuery(id+"F6.wireOp",EDGE,"E28.2.0.1"),sQuery(id+"F6.wireOp",EDGE,"E28.2.0.2"),sQuery(id+"F6.wireOp",EDGE,"E28.2.0.3")])],"isStart":false})});
            var Q94;
            Q94=makeQuery(id+"F7.boolean.opBoolean","COPY",FACE,{"derivedFrom":makeQuery(id+"F7.opExtrude","CAP_FACE",FACE,{"disambiguationData":[OSD([sQuery(id+"F6.wireOp",EDGE,"E28.1.0.0"),sQuery(id+"F6.wireOp",EDGE,"E28.1.0.1"),sQuery(id+"F6.wireOp",EDGE,"E28.1.0.2"),sQuery(id+"F6.wireOp",EDGE,"E28.1.0.3")])],"isStart":false})});
            var Q95;
            Q95=makeQuery(id+"F7.boolean.opBoolean","COPY",FACE,{"derivedFrom":makeQuery(id+"F7.opExtrude","CAP_FACE",FACE,{"disambiguationData":[OSD([sQuery(id+"F6.wireOp",EDGE,"E25.bottom"),sQuery(id+"F6.wireOp",EDGE,"E25.top"),sQuery(id+"F6.wireOp",EDGE,"E25.left"),sQuery(id+"F6.wireOp",EDGE,"E25.right")])],"isStart":false})});
            var Q96;
            Q96=makeQuery(id+"F7.boolean.opBoolean","COPY",FACE,{"derivedFrom":makeQuery(id+"F7.opExtrude","CAP_FACE",FACE,{"disambiguationData":[OSD([sQuery(id+"F6.wireOp",EDGE,"E27.1.0.0"),sQuery(id+"F6.wireOp",EDGE,"E27.1.0.1"),sQuery(id+"F6.wireOp",EDGE,"E27.1.0.2"),sQuery(id+"F6.wireOp",EDGE,"E27.1.0.3")])],"isStart":false})});
            var Q97;
            Q97=makeQuery(id+"F7.boolean.opBoolean","COPY",FACE,{"derivedFrom":makeQuery(id+"F7.opExtrude","CAP_FACE",FACE,{"disambiguationData":[OSD([sQuery(id+"F6.wireOp",EDGE,"E27.2.0.0"),sQuery(id+"F6.wireOp",EDGE,"E27.2.0.1"),sQuery(id+"F6.wireOp",EDGE,"E27.2.0.2"),sQuery(id+"F6.wireOp",EDGE,"E27.2.0.3")])],"isStart":false})});
            var Q98;
            Q98=makeQuery(id+"F7.boolean.opBoolean","COPY",FACE,{"derivedFrom":makeQuery(id+"F7.opExtrude","CAP_FACE",FACE,{"disambiguationData":[OSD([sQuery(id+"F6.wireOp",EDGE,"E27.3.0.0"),sQuery(id+"F6.wireOp",EDGE,"E27.3.0.1"),sQuery(id+"F6.wireOp",EDGE,"E27.3.0.2"),sQuery(id+"F6.wireOp",EDGE,"E27.3.0.3")])],"isStart":false})});
            var Q99;
            Q99=makeQuery(id+"F7.boolean.opBoolean","COPY",FACE,{"derivedFrom":makeQuery(id+"F7.opExtrude","CAP_FACE",FACE,{"disambiguationData":[OSD([sQuery(id+"F6.wireOp",EDGE,"E27.4.0.0"),sQuery(id+"F6.wireOp",EDGE,"E27.4.0.1"),sQuery(id+"F6.wireOp",EDGE,"E27.4.0.2"),sQuery(id+"F6.wireOp",EDGE,"E27.4.0.3")])],"isStart":false})});
            var Q100;
            Q100=makeQuery(id+"F7.boolean.opBoolean","COPY",FACE,{"derivedFrom":makeQuery(id+"F7.opExtrude","CAP_FACE",FACE,{"disambiguationData":[OSD([sQuery(id+"F6.wireOp",EDGE,"E27.5.0.0"),sQuery(id+"F6.wireOp",EDGE,"E27.5.0.1"),sQuery(id+"F6.wireOp",EDGE,"E27.5.0.2"),sQuery(id+"F6.wireOp",EDGE,"E27.5.0.3")])],"isStart":false})});
            var Q101;
            Q101=makeQuery(id+"F7.boolean.opBoolean","COPY",FACE,{"derivedFrom":makeQuery(id+"F7.opExtrude","CAP_FACE",FACE,{"disambiguationData":[OSD([sQuery(id+"F6.wireOp",EDGE,"E27.6.0.0"),sQuery(id+"F6.wireOp",EDGE,"E27.6.0.1"),sQuery(id+"F6.wireOp",EDGE,"E27.6.0.2"),sQuery(id+"F6.wireOp",EDGE,"E27.6.0.3")])],"isStart":false})});
            var Q102;
            Q102=makeQuery(id+"F7.boolean.opBoolean","COPY",FACE,{"derivedFrom":makeQuery(id+"F7.opExtrude","CAP_FACE",FACE,{"disambiguationData":[OSD([sQuery(id+"F6.wireOp",EDGE,"E27.7.0.0"),sQuery(id+"F6.wireOp",EDGE,"E27.7.0.1"),sQuery(id+"F6.wireOp",EDGE,"E27.7.0.2"),sQuery(id+"F6.wireOp",EDGE,"E27.7.0.3")])],"isStart":false})});
            var Q103;
            Q103=makeQuery(id+"F7.boolean.opBoolean","COPY",FACE,{"derivedFrom":makeQuery(id+"F7.opExtrude","CAP_FACE",FACE,{"disambiguationData":[OSD([sQuery(id+"F6.wireOp",EDGE,"E27.8.0.0"),sQuery(id+"F6.wireOp",EDGE,"E27.8.0.1"),sQuery(id+"F6.wireOp",EDGE,"E27.8.0.2"),sQuery(id+"F6.wireOp",EDGE,"E27.8.0.3")])],"isStart":false})});
            var Q104;
            Q104=makeQuery(id+"F7.boolean.opBoolean","COPY",FACE,{"derivedFrom":makeQuery(id+"F7.opExtrude","CAP_FACE",FACE,{"disambiguationData":[OSD([sQuery(id+"F6.wireOp",EDGE,"E27.9.0.0"),sQuery(id+"F6.wireOp",EDGE,"E27.9.0.1"),sQuery(id+"F6.wireOp",EDGE,"E27.9.0.2"),sQuery(id+"F6.wireOp",EDGE,"E27.9.0.3")])],"isStart":false})});
            var Q105;
            Q105=makeQuery(id+"F7.boolean.opBoolean","COPY",FACE,{"derivedFrom":makeQuery(id+"F7.opExtrude","CAP_FACE",FACE,{"disambiguationData":[OSD([sQuery(id+"F6.wireOp",EDGE,"E34.1.0.16"),sQuery(id+"F6.wireOp",EDGE,"E34.1.0.18"),sQuery(id+"F6.wireOp",EDGE,"E34.1.0.19"),sQuery(id+"F6.wireOp",EDGE,"E34.1.0.20")])],"isStart":false})});
            extrude(context, id + "F8", {"entities" : qUnion([Q0, Q1, Q2, Q3, Q4, Q5, Q6, Q7, Q8, Q9, Q10, Q11, Q12, Q13, Q14, Q15, Q16, Q17, Q18, Q19, Q20, Q21, Q22, Q23, Q24, Q25, Q26, Q27, Q28, Q29, Q30, Q31, Q32, Q33, Q34, Q35, Q36, Q37, Q38, Q39, Q40, Q41, Q42, Q43, Q44, Q45, Q46, Q47, Q48, Q49, Q50, Q51, Q52, Q53, Q54, Q55, Q56, Q57, Q58, Q59, Q60, Q61, Q62, Q63, Q64, Q65, Q66, Q67, Q68, Q69, Q70, Q71, Q72, Q73, Q74, Q75, Q76, Q77, Q78, Q79, Q80, Q81, Q82, Q83, Q84, Q85, Q86, Q87, Q88, Q89, Q90, Q91, Q92, Q93, Q94, Q95, Q96, Q97, Q98, Q99, Q100, Q101, Q102, Q103, Q104, Q105]), "depth" : 0.03 * mm});
        }
        {
            var Q0;
            Q0=makeQuery(id+"F7.boolean.opBoolean","COPY",FACE,{"derivedFrom":makeQuery(id+"F7.opExtrude","CAP_FACE",FACE,{"disambiguationData":[OSD([sQuery(id+"F6.wireOp",EDGE,"E33.1.0.11"),sQuery(id+"F6.wireOp",EDGE,"E33.1.0.12"),sQuery(id+"F6.wireOp",EDGE,"E33.1.0.15"),sQuery(id+"F6.wireOp",EDGE,"E33.1.0.17")])],"isStart":false})});
            extrude(context, id + "F9", {"entities" : qUnion([Q0]), "depth" : 0.03 * mm});
        }
        {
            var Q0;
            Q0=makeQuery(id+"F1.opExtrude","CAP_FACE",FACE,{"disambiguationData":[OSD([sQuery(id+"F0.wireOp",EDGE,"E0.bottom"),sQuery(id+"F0.wireOp",EDGE,"E0.top"),sQuery(id+"F0.wireOp",EDGE,"E0.left"),sQuery(id+"F0.wireOp",EDGE,"E0.right"),sQuery(id+"F0.wireOp",EDGE,"E1")])],"isStart":false});
            var sketch = newSketch(context, id + "F10", { "sketchPlane" : qUnion([Q0])});
            skText(sketch, "E52", { "text": "CINTERION", "fontName": "OpenSans-Regular.ttf"});
            skText(sketch, "E53", { "text": "Model :  EHS5-E", "fontName": "OpenSans-Regular.ttf"});
            skLineSegment(sketch, "E54", {"start": v(-5.23, -1.08) * mm, "end": v(-8.43, -1.08) * mm});
            skFitSpline(sketch, "E55", {"points": [v(-6.26, -2.43) * mm, v(-6.55, -2.6) * mm, v(-7.03, -2.59) * mm, v(-7.27, -2.6) * mm, v(-7.46, -2.76) * mm], "startDerivative": vector(-1, -0.9) * mm, "endDerivative": vector(-0.85, -0.83) * mm});
            skFitSpline(sketch, "E56", {"points": [v(-7.04, -1.97) * mm, v(-7.6, -2.4) * mm, v(-7.7, -2.37) * mm], "startDerivative": vector(-0.9, -0.81) * mm, "endDerivative": vector(-0.29, 0.17) * mm});
            skLineSegment(sketch, "E57", {"start": v(-6.2, -2.37) * mm, "end": v(-5.97, -1.95) * mm});
            skLineSegment(sketch, "E58", {"start": v(-5.97, -1.95) * mm, "end": v(-6.3, -1.35) * mm});
            skFitSpline(sketch, "E59", {"points": [v(-6.3, -1.35) * mm, v(-6.22, -1.96) * mm, v(-6.43, -2.24) * mm], "startDerivative": vector(0.32, -1.2) * mm, "endDerivative": vector(-0.63, -0.55) * mm});
            skLineSegment(sketch, "E60", {"start": v(-7, -1.91) * mm, "end": v(-6.58, -1.35) * mm});
            skLineSegment(sketch, "E61", {"start": v(-6.58, -1.35) * mm, "end": v(-6.53, -1.6) * mm});
            skLineSegment(sketch, "E62", {"start": v(-6.53, -1.6) * mm, "end": v(-6.87, -1.99) * mm});
            skLineSegment(sketch, "E63", {"start": v(-6.07, -2.53) * mm, "end": v(-6.26, -2.43) * mm});
            skLineSegment(sketch, "E64", {"start": v(-7.04, -1.97) * mm, "end": v(-8.36, -1.21) * mm});
            skLineSegment(sketch, "E65", {"start": v(-7.7, -2.37) * mm, "end": v(-8.36, -1.21) * mm});
            skLineSegment(sketch, "E66", {"start": v(-7.46, -2.76) * mm, "end": v(-6.83, -3.86) * mm});
            skLineSegment(sketch, "E67", {"start": v(-6.07, -2.53) * mm, "end": v(-6.83, -3.86) * mm});
            skLineSegment(sketch, "E68", {"start": v(-6.2, -2.37) * mm, "end": v(-6.03, -2.47) * mm});
            skLineSegment(sketch, "E69", {"start": v(-6.43, -2.24) * mm, "end": v(-6.87, -1.99) * mm});
            skLineSegment(sketch, "E70", {"start": v(-7, -1.91) * mm, "end": v(-8.43, -1.08) * mm});
            skLineSegment(sketch, "E71", {"start": v(-8.43, -1.08) * mm, "end": v(-5.23, -1.08) * mm});
            skLineSegment(sketch, "E72", {"start": v(-5.23, -1.08) * mm, "end": v(-6.03, -2.47) * mm});
            const initialGuessF10  = {"E52": [0.01196, -0.00553, -1, 0, 0.00155], "E53": [0.01194, -0.00187, -1, 0, 0.00087]};
            skSetInitialGuess(sketch, initialGuessF10);
            skSolve(sketch);
        }
        {
            var Q0;
            Q0 = qSketchRegion(id + "F10", true);
            extrude(context, id + "F11", {"entities" : qUnion([Q0]), "depth" : 0 * mm});
        }
    });
